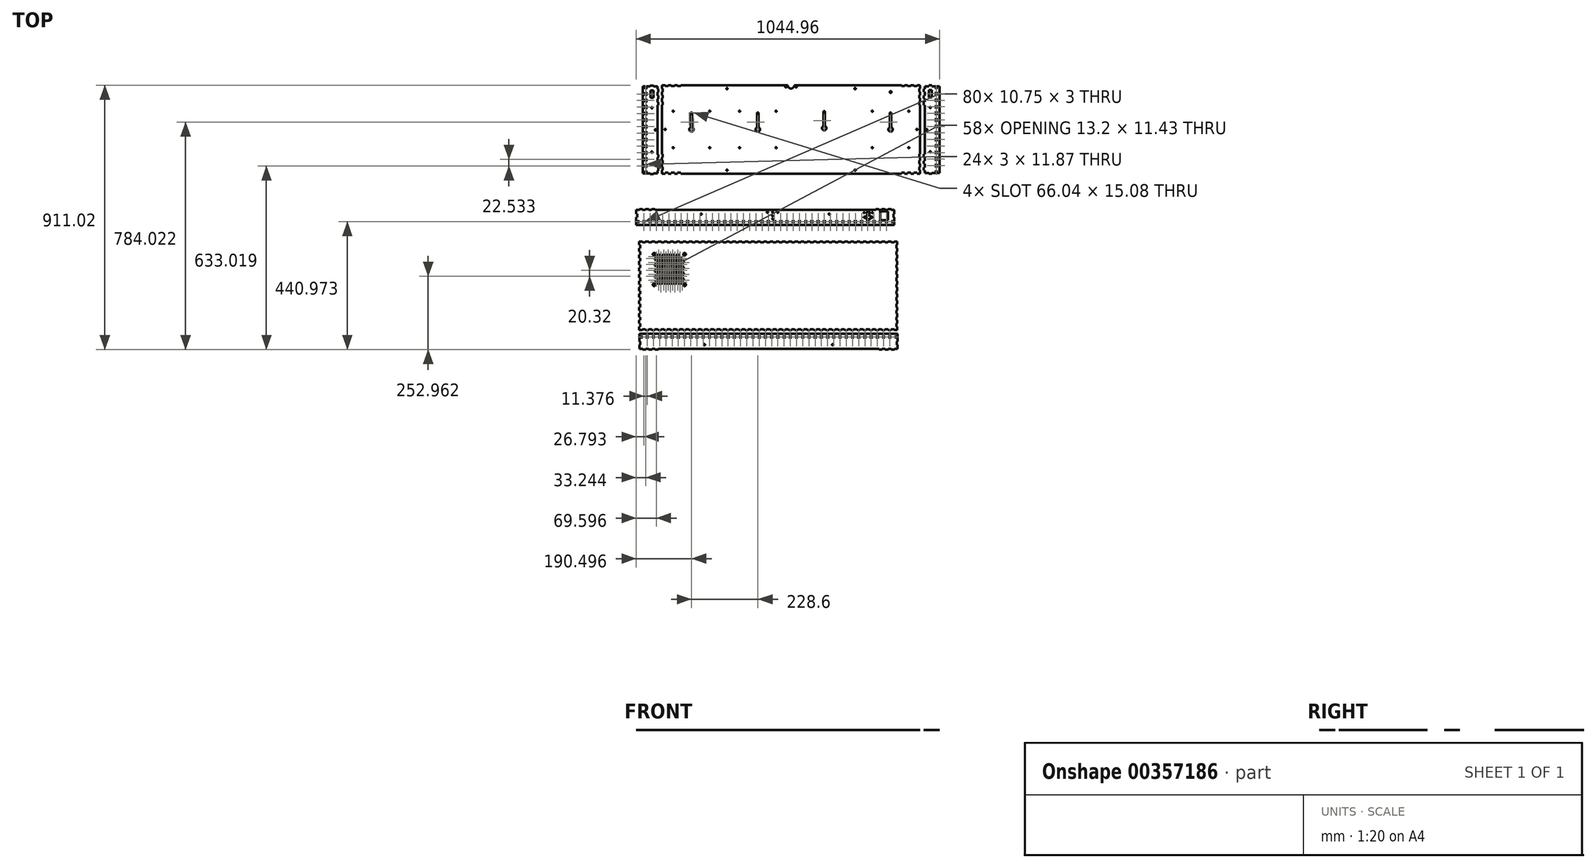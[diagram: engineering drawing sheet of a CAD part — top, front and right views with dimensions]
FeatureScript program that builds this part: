
annotation { "Feature Type Name" : "Feature", "Feature Type Description" : "" }
export const myFeature = defineFeature(function(context is Context, id is Id, definition is map)
    precondition{}
    {
        {
            var Q0;
            Q0=qCreatedBy(makeId("Top.planeOp"),FACE);
            var sketch = newSketch(context, id + "F0", { "sketchPlane" : qUnion([Q0])});
            skLineSegment(sketch, "E0", {"start": v(-511.9, -83.35) * mm, "end": v(-501.15, -83.35) * mm});
            skLineSegment(sketch, "E1", {"start": v(-501.15, -83.35) * mm, "end": v(-501.15, -86.34) * mm});
            skLineSegment(sketch, "E2", {"start": v(-501.15, -86.34) * mm, "end": v(-490.48, -86.34) * mm});
            skLineSegment(sketch, "E3", {"start": v(-490.48, -86.34) * mm, "end": v(-490.48, -83.35) * mm});
            skLineSegment(sketch, "E4", {"start": v(-490.48, -83.35) * mm, "end": v(-479.73, -83.35) * mm});
            skLineSegment(sketch, "E5", {"start": v(-479.73, -83.35) * mm, "end": v(-479.73, -86.34) * mm});
            skLineSegment(sketch, "E6", {"start": v(-479.73, -86.34) * mm, "end": v(-469.06, -86.34) * mm});
            skLineSegment(sketch, "E7", {"start": v(-469.06, -86.34) * mm, "end": v(-469.06, -83.35) * mm});
            skLineSegment(sketch, "E8", {"start": v(-469.06, -83.35) * mm, "end": v(-458.3, -83.35) * mm});
            skLineSegment(sketch, "E9", {"start": v(-458.3, -83.35) * mm, "end": v(-458.3, -86.34) * mm});
            skLineSegment(sketch, "E10", {"start": v(-458.3, -86.34) * mm, "end": v(-447.64, -86.34) * mm});
            skLineSegment(sketch, "E11", {"start": v(-447.64, -86.34) * mm, "end": v(-447.64, -83.35) * mm});
            skLineSegment(sketch, "E12", {"start": v(-447.64, -83.35) * mm, "end": v(-436.89, -83.35) * mm});
            skLineSegment(sketch, "E13", {"start": v(-436.89, -83.35) * mm, "end": v(-436.89, -86.34) * mm});
            skLineSegment(sketch, "E14", {"start": v(-436.89, -86.34) * mm, "end": v(-426.22, -86.34) * mm});
            skLineSegment(sketch, "E15", {"start": v(-426.22, -86.34) * mm, "end": v(-426.22, -83.35) * mm});
            skLineSegment(sketch, "E16", {"start": v(-426.22, -83.35) * mm, "end": v(-415.47, -83.35) * mm});
            skLineSegment(sketch, "E17", {"start": v(-415.47, -83.35) * mm, "end": v(-415.47, -86.34) * mm});
            skLineSegment(sketch, "E18", {"start": v(-415.47, -86.34) * mm, "end": v(-404.8, -86.34) * mm});
            skLineSegment(sketch, "E19", {"start": v(-404.8, -86.34) * mm, "end": v(-404.8, -83.35) * mm});
            skLineSegment(sketch, "E20", {"start": v(-404.8, -83.35) * mm, "end": v(-394.05, -83.35) * mm});
            skLineSegment(sketch, "E21", {"start": v(-394.05, -83.35) * mm, "end": v(-394.05, -86.34) * mm});
            skLineSegment(sketch, "E22", {"start": v(-394.05, -86.34) * mm, "end": v(-383.38, -86.34) * mm});
            skLineSegment(sketch, "E23", {"start": v(-383.38, -86.34) * mm, "end": v(-383.38, -83.35) * mm});
            skLineSegment(sketch, "E24", {"start": v(-383.38, -83.35) * mm, "end": v(-372.62, -83.35) * mm});
            skLineSegment(sketch, "E25", {"start": v(-372.62, -83.35) * mm, "end": v(-372.62, -86.34) * mm});
            skLineSegment(sketch, "E26", {"start": v(-372.62, -86.34) * mm, "end": v(-361.96, -86.34) * mm});
            skLineSegment(sketch, "E27", {"start": v(-361.96, -86.34) * mm, "end": v(-361.96, -83.35) * mm});
            skLineSegment(sketch, "E28", {"start": v(-361.96, -83.35) * mm, "end": v(-351.2, -83.35) * mm});
            skLineSegment(sketch, "E29", {"start": v(-351.2, -83.35) * mm, "end": v(-351.2, -86.34) * mm});
            skLineSegment(sketch, "E30", {"start": v(-351.2, -86.34) * mm, "end": v(-340.54, -86.34) * mm});
            skLineSegment(sketch, "E31", {"start": v(-340.54, -86.34) * mm, "end": v(-340.54, -83.35) * mm});
            skLineSegment(sketch, "E32", {"start": v(-340.54, -83.35) * mm, "end": v(-329.78, -83.35) * mm});
            skLineSegment(sketch, "E33", {"start": v(-329.78, -83.35) * mm, "end": v(-329.78, -86.34) * mm});
            skLineSegment(sketch, "E34", {"start": v(-329.78, -86.34) * mm, "end": v(-319.12, -86.34) * mm});
            skLineSegment(sketch, "E35", {"start": v(-319.12, -86.34) * mm, "end": v(-319.12, -83.35) * mm});
            skLineSegment(sketch, "E36", {"start": v(-319.12, -83.35) * mm, "end": v(-308.36, -83.35) * mm});
            skLineSegment(sketch, "E37", {"start": v(-308.36, -83.35) * mm, "end": v(-308.36, -86.34) * mm});
            skLineSegment(sketch, "E38", {"start": v(-308.36, -86.34) * mm, "end": v(-297.7, -86.34) * mm});
            skLineSegment(sketch, "E39", {"start": v(-297.7, -86.34) * mm, "end": v(-297.7, -83.35) * mm});
            skLineSegment(sketch, "E40", {"start": v(-297.7, -83.35) * mm, "end": v(-286.94, -83.35) * mm});
            skLineSegment(sketch, "E41", {"start": v(-286.94, -83.35) * mm, "end": v(-286.94, -86.34) * mm});
            skLineSegment(sketch, "E42", {"start": v(-286.94, -86.34) * mm, "end": v(-276.27, -86.34) * mm});
            skLineSegment(sketch, "E43", {"start": v(-276.27, -86.34) * mm, "end": v(-276.27, -83.35) * mm});
            skLineSegment(sketch, "E44", {"start": v(-276.27, -83.35) * mm, "end": v(-265.52, -83.35) * mm});
            skLineSegment(sketch, "E45", {"start": v(-265.52, -83.35) * mm, "end": v(-265.52, -86.34) * mm});
            skLineSegment(sketch, "E46", {"start": v(-265.52, -86.34) * mm, "end": v(-254.85, -86.34) * mm});
            skLineSegment(sketch, "E47", {"start": v(-254.85, -86.34) * mm, "end": v(-254.85, -83.35) * mm});
            skLineSegment(sketch, "E48", {"start": v(-254.85, -83.35) * mm, "end": v(-244.1, -83.35) * mm});
            skLineSegment(sketch, "E49", {"start": v(-244.1, -83.35) * mm, "end": v(-244.1, -86.34) * mm});
            skLineSegment(sketch, "E50", {"start": v(-244.1, -86.34) * mm, "end": v(-233.43, -86.34) * mm});
            skLineSegment(sketch, "E51", {"start": v(-233.43, -86.34) * mm, "end": v(-233.43, -83.35) * mm});
            skLineSegment(sketch, "E52", {"start": v(-233.43, -83.35) * mm, "end": v(-222.68, -83.35) * mm});
            skLineSegment(sketch, "E53", {"start": v(-222.68, -83.35) * mm, "end": v(-222.68, -86.34) * mm});
            skLineSegment(sketch, "E54", {"start": v(-222.68, -86.34) * mm, "end": v(-212.01, -86.34) * mm});
            skLineSegment(sketch, "E55", {"start": v(-212.01, -86.34) * mm, "end": v(-212.01, -83.35) * mm});
            skLineSegment(sketch, "E56", {"start": v(-212.01, -83.35) * mm, "end": v(-201.26, -83.35) * mm});
            skLineSegment(sketch, "E57", {"start": v(-201.26, -83.35) * mm, "end": v(-201.26, -86.34) * mm});
            skLineSegment(sketch, "E58", {"start": v(-201.26, -86.34) * mm, "end": v(-190.6, -86.34) * mm});
            skLineSegment(sketch, "E59", {"start": v(-190.6, -86.34) * mm, "end": v(-190.6, -83.35) * mm});
            skLineSegment(sketch, "E60", {"start": v(-190.6, -83.35) * mm, "end": v(-179.84, -83.35) * mm});
            skLineSegment(sketch, "E61", {"start": v(-179.84, -83.35) * mm, "end": v(-179.84, -86.34) * mm});
            skLineSegment(sketch, "E62", {"start": v(-179.84, -86.34) * mm, "end": v(-169.17, -86.34) * mm});
            skLineSegment(sketch, "E63", {"start": v(-169.17, -86.34) * mm, "end": v(-169.17, -83.35) * mm});
            skLineSegment(sketch, "E64", {"start": v(-169.17, -83.35) * mm, "end": v(-158.42, -83.35) * mm});
            skLineSegment(sketch, "E65", {"start": v(-158.42, -83.35) * mm, "end": v(-158.42, -86.34) * mm});
            skLineSegment(sketch, "E66", {"start": v(-158.42, -86.34) * mm, "end": v(-147.75, -86.34) * mm});
            skLineSegment(sketch, "E67", {"start": v(-147.75, -86.34) * mm, "end": v(-147.75, -83.35) * mm});
            skLineSegment(sketch, "E68", {"start": v(-147.75, -83.35) * mm, "end": v(-137, -83.35) * mm});
            skLineSegment(sketch, "E69", {"start": v(-137, -83.35) * mm, "end": v(-137, -86.34) * mm});
            skLineSegment(sketch, "E70", {"start": v(-137, -86.34) * mm, "end": v(-126.33, -86.34) * mm});
            skLineSegment(sketch, "E71", {"start": v(-126.33, -86.34) * mm, "end": v(-126.33, -83.35) * mm});
            skLineSegment(sketch, "E72", {"start": v(-126.33, -83.35) * mm, "end": v(-115.58, -83.35) * mm});
            skLineSegment(sketch, "E73", {"start": v(-115.58, -83.35) * mm, "end": v(-115.58, -86.34) * mm});
            skLineSegment(sketch, "E74", {"start": v(-115.58, -86.34) * mm, "end": v(-104.9, -86.34) * mm});
            skLineSegment(sketch, "E75", {"start": v(-104.9, -86.34) * mm, "end": v(-104.9, -83.35) * mm});
            skLineSegment(sketch, "E76", {"start": v(-104.9, -83.35) * mm, "end": v(-94.16, -83.35) * mm});
            skLineSegment(sketch, "E77", {"start": v(-94.16, -83.35) * mm, "end": v(-94.16, -86.34) * mm});
            skLineSegment(sketch, "E78", {"start": v(-94.16, -86.34) * mm, "end": v(-83.49, -86.34) * mm});
            skLineSegment(sketch, "E79", {"start": v(-83.49, -86.34) * mm, "end": v(-83.49, -83.35) * mm});
            skLineSegment(sketch, "E80", {"start": v(-83.49, -83.35) * mm, "end": v(-72.74, -83.35) * mm});
            skLineSegment(sketch, "E81", {"start": v(-72.74, -83.35) * mm, "end": v(-72.74, -86.34) * mm});
            skLineSegment(sketch, "E82", {"start": v(-72.74, -86.34) * mm, "end": v(-62.07, -86.34) * mm});
            skLineSegment(sketch, "E83", {"start": v(-62.07, -86.34) * mm, "end": v(-62.07, -83.35) * mm});
            skLineSegment(sketch, "E84", {"start": v(-62.07, -83.35) * mm, "end": v(-51.31, -83.35) * mm});
            skLineSegment(sketch, "E85", {"start": v(-51.31, -83.35) * mm, "end": v(-51.31, -86.34) * mm});
            skLineSegment(sketch, "E86", {"start": v(-51.31, -86.34) * mm, "end": v(-40.65, -86.34) * mm});
            skLineSegment(sketch, "E87", {"start": v(-40.65, -86.34) * mm, "end": v(-40.65, -83.35) * mm});
            skLineSegment(sketch, "E88", {"start": v(-40.65, -83.35) * mm, "end": v(-29.9, -83.35) * mm});
            skLineSegment(sketch, "E89", {"start": v(-29.9, -83.35) * mm, "end": v(-29.9, -86.34) * mm});
            skLineSegment(sketch, "E90", {"start": v(-29.9, -86.34) * mm, "end": v(-19.23, -86.34) * mm});
            skLineSegment(sketch, "E91", {"start": v(-19.23, -86.34) * mm, "end": v(-19.23, -83.35) * mm});
            skLineSegment(sketch, "E92", {"start": v(-19.23, -83.35) * mm, "end": v(-8.47, -83.35) * mm});
            skLineSegment(sketch, "E93", {"start": v(-8.47, -83.35) * mm, "end": v(-8.47, -86.34) * mm});
            skLineSegment(sketch, "E94", {"start": v(-8.47, -86.34) * mm, "end": v(2.2, -86.34) * mm});
            skLineSegment(sketch, "E95", {"start": v(2.2, -86.34) * mm, "end": v(2.2, -83.35) * mm});
            skLineSegment(sketch, "E96", {"start": v(2.2, -83.35) * mm, "end": v(12.95, -83.35) * mm});
            skLineSegment(sketch, "E97", {"start": v(12.95, -83.35) * mm, "end": v(12.95, -86.34) * mm});
            skLineSegment(sketch, "E98", {"start": v(12.95, -86.34) * mm, "end": v(23.62, -86.34) * mm});
            skLineSegment(sketch, "E99", {"start": v(23.62, -86.34) * mm, "end": v(23.62, -83.35) * mm});
            skLineSegment(sketch, "E100", {"start": v(23.62, -83.35) * mm, "end": v(34.37, -83.35) * mm});
            skLineSegment(sketch, "E101", {"start": v(34.37, -83.35) * mm, "end": v(34.37, -86.34) * mm});
            skLineSegment(sketch, "E102", {"start": v(34.37, -86.34) * mm, "end": v(45.04, -86.34) * mm});
            skLineSegment(sketch, "E103", {"start": v(45.04, -86.34) * mm, "end": v(45.04, -83.35) * mm});
            skLineSegment(sketch, "E104", {"start": v(45.04, -83.35) * mm, "end": v(55.79, -83.35) * mm});
            skLineSegment(sketch, "E105", {"start": v(55.79, -83.35) * mm, "end": v(55.79, -86.34) * mm});
            skLineSegment(sketch, "E106", {"start": v(55.79, -86.34) * mm, "end": v(66.46, -86.34) * mm});
            skLineSegment(sketch, "E107", {"start": v(66.46, -86.34) * mm, "end": v(66.46, -83.35) * mm});
            skLineSegment(sketch, "E108", {"start": v(66.46, -83.35) * mm, "end": v(77.2, -83.35) * mm});
            skLineSegment(sketch, "E109", {"start": v(77.2, -83.35) * mm, "end": v(77.2, -86.34) * mm});
            skLineSegment(sketch, "E110", {"start": v(77.2, -86.34) * mm, "end": v(87.88, -86.34) * mm});
            skLineSegment(sketch, "E111", {"start": v(87.88, -86.34) * mm, "end": v(87.88, -83.35) * mm});
            skLineSegment(sketch, "E112", {"start": v(87.88, -83.35) * mm, "end": v(98.63, -83.35) * mm});
            skLineSegment(sketch, "E113", {"start": v(98.63, -83.35) * mm, "end": v(98.63, -86.34) * mm});
            skLineSegment(sketch, "E114", {"start": v(98.63, -86.34) * mm, "end": v(109.3, -86.34) * mm});
            skLineSegment(sketch, "E115", {"start": v(109.3, -86.34) * mm, "end": v(109.3, -83.35) * mm});
            skLineSegment(sketch, "E116", {"start": v(109.3, -83.35) * mm, "end": v(120.05, -83.35) * mm});
            skLineSegment(sketch, "E117", {"start": v(120.05, -83.35) * mm, "end": v(120.05, -86.34) * mm});
            skLineSegment(sketch, "E118", {"start": v(120.05, -86.34) * mm, "end": v(130.72, -86.34) * mm});
            skLineSegment(sketch, "E119", {"start": v(130.72, -86.34) * mm, "end": v(130.72, -83.35) * mm});
            skLineSegment(sketch, "E120", {"start": v(130.72, -83.35) * mm, "end": v(141.47, -83.35) * mm});
            skLineSegment(sketch, "E121", {"start": v(141.47, -83.35) * mm, "end": v(141.47, -86.34) * mm});
            skLineSegment(sketch, "E122", {"start": v(141.47, -86.34) * mm, "end": v(152.14, -86.34) * mm});
            skLineSegment(sketch, "E123", {"start": v(152.14, -86.34) * mm, "end": v(152.14, -83.35) * mm});
            skLineSegment(sketch, "E124", {"start": v(152.14, -83.35) * mm, "end": v(162.9, -83.35) * mm});
            skLineSegment(sketch, "E125", {"start": v(162.9, -83.35) * mm, "end": v(162.9, -86.34) * mm});
            skLineSegment(sketch, "E126", {"start": v(162.9, -86.34) * mm, "end": v(173.56, -86.34) * mm});
            skLineSegment(sketch, "E127", {"start": v(173.56, -86.34) * mm, "end": v(173.56, -83.35) * mm});
            skLineSegment(sketch, "E128", {"start": v(173.56, -83.35) * mm, "end": v(184.31, -83.35) * mm});
            skLineSegment(sketch, "E129", {"start": v(184.31, -83.35) * mm, "end": v(184.31, -86.34) * mm});
            skLineSegment(sketch, "E130", {"start": v(184.31, -86.34) * mm, "end": v(194.98, -86.34) * mm});
            skLineSegment(sketch, "E131", {"start": v(194.98, -86.34) * mm, "end": v(194.98, -83.35) * mm});
            skLineSegment(sketch, "E132", {"start": v(194.98, -83.35) * mm, "end": v(205.73, -83.35) * mm});
            skLineSegment(sketch, "E133", {"start": v(205.73, -83.35) * mm, "end": v(205.73, -86.34) * mm});
            skLineSegment(sketch, "E134", {"start": v(205.73, -86.34) * mm, "end": v(216.4, -86.34) * mm});
            skLineSegment(sketch, "E135", {"start": v(216.4, -86.34) * mm, "end": v(216.4, -83.35) * mm});
            skLineSegment(sketch, "E136", {"start": v(216.4, -83.35) * mm, "end": v(227.15, -83.35) * mm});
            skLineSegment(sketch, "E137", {"start": v(227.15, -83.35) * mm, "end": v(227.15, -86.34) * mm});
            skLineSegment(sketch, "E138", {"start": v(227.15, -86.34) * mm, "end": v(237.82, -86.34) * mm});
            skLineSegment(sketch, "E139", {"start": v(237.82, -86.34) * mm, "end": v(237.82, -83.35) * mm});
            skLineSegment(sketch, "E140", {"start": v(237.82, -83.35) * mm, "end": v(248.57, -83.35) * mm});
            skLineSegment(sketch, "E141", {"start": v(248.57, -83.35) * mm, "end": v(248.57, -86.34) * mm});
            skLineSegment(sketch, "E142", {"start": v(248.57, -86.34) * mm, "end": v(259.24, -86.34) * mm});
            skLineSegment(sketch, "E143", {"start": v(259.24, -86.34) * mm, "end": v(259.24, -83.35) * mm});
            skLineSegment(sketch, "E144", {"start": v(259.24, -83.35) * mm, "end": v(270, -83.35) * mm});
            skLineSegment(sketch, "E145", {"start": v(270, -83.35) * mm, "end": v(270, -86.34) * mm});
            skLineSegment(sketch, "E146", {"start": v(270, -86.34) * mm, "end": v(280.66, -86.34) * mm});
            skLineSegment(sketch, "E147", {"start": v(280.66, -86.34) * mm, "end": v(280.66, -83.35) * mm});
            skLineSegment(sketch, "E148", {"start": v(280.66, -83.35) * mm, "end": v(291.42, -83.35) * mm});
            skLineSegment(sketch, "E149", {"start": v(291.42, -83.35) * mm, "end": v(291.42, -86.34) * mm});
            skLineSegment(sketch, "E150", {"start": v(291.42, -86.34) * mm, "end": v(302.08, -86.34) * mm});
            skLineSegment(sketch, "E151", {"start": v(302.08, -86.34) * mm, "end": v(302.08, -83.35) * mm});
            skLineSegment(sketch, "E152", {"start": v(302.08, -83.35) * mm, "end": v(312.84, -83.35) * mm});
            skLineSegment(sketch, "E153", {"start": v(312.84, -83.35) * mm, "end": v(312.84, -86.34) * mm});
            skLineSegment(sketch, "E154", {"start": v(312.84, -86.34) * mm, "end": v(323.5, -86.34) * mm});
            skLineSegment(sketch, "E155", {"start": v(323.5, -86.34) * mm, "end": v(323.5, -83.35) * mm});
            skLineSegment(sketch, "E156", {"start": v(323.5, -83.35) * mm, "end": v(334.26, -83.35) * mm});
            skLineSegment(sketch, "E157", {"start": v(334.26, -83.35) * mm, "end": v(334.26, -86.34) * mm});
            skLineSegment(sketch, "E158", {"start": v(334.26, -86.34) * mm, "end": v(344.93, -86.34) * mm});
            skLineSegment(sketch, "E159", {"start": v(344.93, -86.34) * mm, "end": v(344.93, -83.35) * mm});
            skLineSegment(sketch, "E160", {"start": v(344.93, -83.35) * mm, "end": v(355.68, -83.35) * mm});
            skLineSegment(sketch, "E161", {"start": v(355.68, -83.35) * mm, "end": v(355.68, -86.34) * mm});
            skLineSegment(sketch, "E162", {"start": v(355.68, -86.34) * mm, "end": v(366.35, -86.34) * mm});
            skLineSegment(sketch, "E163", {"start": v(366.35, -86.34) * mm, "end": v(366.35, -83.35) * mm});
            skLineSegment(sketch, "E164", {"start": v(366.35, -83.35) * mm, "end": v(377.1, -83.35) * mm});
            skLineSegment(sketch, "E165", {"start": v(377.1, -83.35) * mm, "end": v(377.1, -95.21) * mm});
            skLineSegment(sketch, "E166", {"start": v(377.1, -95.21) * mm, "end": v(374.1, -95.21) * mm});
            skLineSegment(sketch, "E167", {"start": v(374.1, -95.21) * mm, "end": v(374.1, -105.88) * mm});
            skLineSegment(sketch, "E168", {"start": v(374.1, -105.88) * mm, "end": v(377.1, -105.88) * mm});
            skLineSegment(sketch, "E169", {"start": v(377.1, -105.88) * mm, "end": v(377.1, -117.75) * mm});
            skLineSegment(sketch, "E170", {"start": v(377.1, -117.75) * mm, "end": v(374.1, -117.75) * mm});
            skLineSegment(sketch, "E171", {"start": v(374.1, -117.75) * mm, "end": v(374.1, -128.41) * mm});
            skLineSegment(sketch, "E172", {"start": v(374.1, -128.41) * mm, "end": v(377.1, -128.41) * mm});
            skLineSegment(sketch, "E173", {"start": v(377.1, -128.41) * mm, "end": v(377.1, -140.28) * mm});
            skLineSegment(sketch, "E174", {"start": v(377.1, -140.28) * mm, "end": v(374.1, -140.28) * mm});
            skLineSegment(sketch, "E175", {"start": v(374.1, -140.28) * mm, "end": v(374.1, -150.95) * mm});
            skLineSegment(sketch, "E176", {"start": v(374.1, -150.95) * mm, "end": v(377.1, -150.95) * mm});
            skLineSegment(sketch, "E177", {"start": v(377.1, -150.95) * mm, "end": v(377.1, -162.81) * mm});
            skLineSegment(sketch, "E178", {"start": v(377.1, -162.81) * mm, "end": v(374.1, -162.81) * mm});
            skLineSegment(sketch, "E179", {"start": v(374.1, -162.81) * mm, "end": v(374.1, -173.48) * mm});
            skLineSegment(sketch, "E180", {"start": v(374.1, -173.48) * mm, "end": v(377.1, -173.48) * mm});
            skLineSegment(sketch, "E181", {"start": v(377.1, -173.48) * mm, "end": v(377.1, -185.35) * mm});
            skLineSegment(sketch, "E182", {"start": v(377.1, -185.35) * mm, "end": v(374.1, -185.35) * mm});
            skLineSegment(sketch, "E183", {"start": v(374.1, -185.35) * mm, "end": v(374.1, -196.01) * mm});
            skLineSegment(sketch, "E184", {"start": v(374.1, -196.01) * mm, "end": v(377.1, -196.01) * mm});
            skLineSegment(sketch, "E185", {"start": v(377.1, -196.01) * mm, "end": v(377.1, -207.88) * mm});
            skLineSegment(sketch, "E186", {"start": v(377.1, -207.88) * mm, "end": v(374.1, -207.88) * mm});
            skLineSegment(sketch, "E187", {"start": v(374.1, -207.88) * mm, "end": v(374.1, -218.55) * mm});
            skLineSegment(sketch, "E188", {"start": v(374.1, -218.55) * mm, "end": v(377.1, -218.55) * mm});
            skLineSegment(sketch, "E189", {"start": v(377.1, -218.55) * mm, "end": v(377.1, -230.41) * mm});
            skLineSegment(sketch, "E190", {"start": v(377.1, -230.41) * mm, "end": v(374.1, -230.41) * mm});
            skLineSegment(sketch, "E191", {"start": v(374.1, -230.41) * mm, "end": v(374.1, -241.08) * mm});
            skLineSegment(sketch, "E192", {"start": v(374.1, -241.08) * mm, "end": v(377.1, -241.08) * mm});
            skLineSegment(sketch, "E193", {"start": v(377.1, -241.08) * mm, "end": v(377.1, -252.95) * mm});
            skLineSegment(sketch, "E194", {"start": v(377.1, -252.95) * mm, "end": v(374.1, -252.95) * mm});
            skLineSegment(sketch, "E195", {"start": v(374.1, -252.95) * mm, "end": v(374.1, -263.61) * mm});
            skLineSegment(sketch, "E196", {"start": v(374.1, -263.61) * mm, "end": v(377.1, -263.61) * mm});
            skLineSegment(sketch, "E197", {"start": v(377.1, -263.61) * mm, "end": v(377.1, -275.48) * mm});
            skLineSegment(sketch, "E198", {"start": v(377.1, -275.48) * mm, "end": v(374.1, -275.48) * mm});
            skLineSegment(sketch, "E199", {"start": v(374.1, -275.48) * mm, "end": v(374.1, -286.15) * mm});
            skLineSegment(sketch, "E200", {"start": v(374.1, -286.15) * mm, "end": v(377.1, -286.15) * mm});
            skLineSegment(sketch, "E201", {"start": v(377.1, -286.15) * mm, "end": v(377.1, -298.01) * mm});
            skLineSegment(sketch, "E202", {"start": v(377.1, -298.01) * mm, "end": v(374.1, -298.01) * mm});
            skLineSegment(sketch, "E203", {"start": v(374.1, -298.01) * mm, "end": v(374.1, -308.68) * mm});
            skLineSegment(sketch, "E204", {"start": v(374.1, -308.68) * mm, "end": v(377.1, -308.68) * mm});
            skLineSegment(sketch, "E205", {"start": v(377.1, -308.68) * mm, "end": v(377.1, -320.55) * mm});
            skLineSegment(sketch, "E206", {"start": v(377.1, -320.55) * mm, "end": v(374.1, -320.55) * mm});
            skLineSegment(sketch, "E207", {"start": v(374.1, -320.55) * mm, "end": v(374.1, -331.22) * mm});
            skLineSegment(sketch, "E208", {"start": v(374.1, -331.22) * mm, "end": v(377.1, -331.22) * mm});
            skLineSegment(sketch, "E209", {"start": v(377.1, -331.22) * mm, "end": v(377.1, -343.08) * mm});
            skLineSegment(sketch, "E210", {"start": v(377.1, -343.08) * mm, "end": v(374.1, -343.08) * mm});
            skLineSegment(sketch, "E211", {"start": v(374.1, -343.08) * mm, "end": v(374.1, -353.75) * mm});
            skLineSegment(sketch, "E212", {"start": v(374.1, -353.75) * mm, "end": v(377.1, -353.75) * mm});
            skLineSegment(sketch, "E213", {"start": v(377.1, -353.75) * mm, "end": v(377.1, -365.61) * mm});
            skLineSegment(sketch, "E214", {"start": v(377.1, -365.61) * mm, "end": v(374.1, -365.61) * mm});
            skLineSegment(sketch, "E215", {"start": v(374.1, -365.61) * mm, "end": v(374.1, -376.28) * mm});
            skLineSegment(sketch, "E216", {"start": v(374.1, -376.28) * mm, "end": v(377.1, -376.28) * mm});
            skLineSegment(sketch, "E217", {"start": v(377.1, -376.28) * mm, "end": v(377.1, -388.15) * mm});
            skLineSegment(sketch, "E218", {"start": v(377.1, -388.15) * mm, "end": v(366.35, -388.15) * mm});
            skLineSegment(sketch, "E219", {"start": v(366.35, -388.15) * mm, "end": v(366.35, -385.15) * mm});
            skLineSegment(sketch, "E220", {"start": v(366.35, -385.15) * mm, "end": v(355.68, -385.15) * mm});
            skLineSegment(sketch, "E221", {"start": v(355.68, -385.15) * mm, "end": v(355.68, -388.15) * mm});
            skLineSegment(sketch, "E222", {"start": v(355.68, -388.15) * mm, "end": v(344.93, -388.15) * mm});
            skLineSegment(sketch, "E223", {"start": v(344.93, -388.15) * mm, "end": v(344.93, -385.15) * mm});
            skLineSegment(sketch, "E224", {"start": v(344.93, -385.15) * mm, "end": v(334.26, -385.15) * mm});
            skLineSegment(sketch, "E225", {"start": v(334.26, -385.15) * mm, "end": v(334.26, -388.15) * mm});
            skLineSegment(sketch, "E226", {"start": v(334.26, -388.15) * mm, "end": v(323.5, -388.15) * mm});
            skLineSegment(sketch, "E227", {"start": v(323.5, -388.15) * mm, "end": v(323.5, -385.15) * mm});
            skLineSegment(sketch, "E228", {"start": v(323.5, -385.15) * mm, "end": v(312.84, -385.15) * mm});
            skLineSegment(sketch, "E229", {"start": v(312.84, -385.15) * mm, "end": v(312.84, -388.15) * mm});
            skLineSegment(sketch, "E230", {"start": v(312.84, -388.15) * mm, "end": v(302.08, -388.15) * mm});
            skLineSegment(sketch, "E231", {"start": v(302.08, -388.15) * mm, "end": v(302.08, -385.15) * mm});
            skLineSegment(sketch, "E232", {"start": v(302.08, -385.15) * mm, "end": v(291.42, -385.15) * mm});
            skLineSegment(sketch, "E233", {"start": v(291.42, -385.15) * mm, "end": v(291.42, -388.15) * mm});
            skLineSegment(sketch, "E234", {"start": v(291.42, -388.15) * mm, "end": v(280.66, -388.15) * mm});
            skLineSegment(sketch, "E235", {"start": v(280.66, -388.15) * mm, "end": v(280.66, -385.15) * mm});
            skLineSegment(sketch, "E236", {"start": v(280.66, -385.15) * mm, "end": v(270, -385.15) * mm});
            skLineSegment(sketch, "E237", {"start": v(270, -385.15) * mm, "end": v(270, -388.15) * mm});
            skLineSegment(sketch, "E238", {"start": v(270, -388.15) * mm, "end": v(259.24, -388.15) * mm});
            skLineSegment(sketch, "E239", {"start": v(259.24, -388.15) * mm, "end": v(259.24, -385.15) * mm});
            skLineSegment(sketch, "E240", {"start": v(259.24, -385.15) * mm, "end": v(248.57, -385.15) * mm});
            skLineSegment(sketch, "E241", {"start": v(248.57, -385.15) * mm, "end": v(248.57, -388.15) * mm});
            skLineSegment(sketch, "E242", {"start": v(248.57, -388.15) * mm, "end": v(237.82, -388.15) * mm});
            skLineSegment(sketch, "E243", {"start": v(237.82, -388.15) * mm, "end": v(237.82, -385.15) * mm});
            skLineSegment(sketch, "E244", {"start": v(237.82, -385.15) * mm, "end": v(227.15, -385.15) * mm});
            skLineSegment(sketch, "E245", {"start": v(227.15, -385.15) * mm, "end": v(227.15, -388.15) * mm});
            skLineSegment(sketch, "E246", {"start": v(227.15, -388.15) * mm, "end": v(216.4, -388.15) * mm});
            skLineSegment(sketch, "E247", {"start": v(216.4, -388.15) * mm, "end": v(216.4, -385.15) * mm});
            skLineSegment(sketch, "E248", {"start": v(216.4, -385.15) * mm, "end": v(205.73, -385.15) * mm});
            skLineSegment(sketch, "E249", {"start": v(205.73, -385.15) * mm, "end": v(205.73, -388.15) * mm});
            skLineSegment(sketch, "E250", {"start": v(205.73, -388.15) * mm, "end": v(194.98, -388.15) * mm});
            skLineSegment(sketch, "E251", {"start": v(194.98, -388.15) * mm, "end": v(194.98, -385.15) * mm});
            skLineSegment(sketch, "E252", {"start": v(194.98, -385.15) * mm, "end": v(184.31, -385.15) * mm});
            skLineSegment(sketch, "E253", {"start": v(184.31, -385.15) * mm, "end": v(184.31, -388.15) * mm});
            skLineSegment(sketch, "E254", {"start": v(184.31, -388.15) * mm, "end": v(173.56, -388.15) * mm});
            skLineSegment(sketch, "E255", {"start": v(173.56, -388.15) * mm, "end": v(173.56, -385.15) * mm});
            skLineSegment(sketch, "E256", {"start": v(173.56, -385.15) * mm, "end": v(162.9, -385.15) * mm});
            skLineSegment(sketch, "E257", {"start": v(162.9, -385.15) * mm, "end": v(162.9, -388.15) * mm});
            skLineSegment(sketch, "E258", {"start": v(162.9, -388.15) * mm, "end": v(152.14, -388.15) * mm});
            skLineSegment(sketch, "E259", {"start": v(152.14, -388.15) * mm, "end": v(152.14, -385.15) * mm});
            skLineSegment(sketch, "E260", {"start": v(152.14, -385.15) * mm, "end": v(141.47, -385.15) * mm});
            skLineSegment(sketch, "E261", {"start": v(141.47, -385.15) * mm, "end": v(141.47, -388.15) * mm});
            skLineSegment(sketch, "E262", {"start": v(141.47, -388.15) * mm, "end": v(130.72, -388.15) * mm});
            skLineSegment(sketch, "E263", {"start": v(130.72, -388.15) * mm, "end": v(130.72, -385.15) * mm});
            skLineSegment(sketch, "E264", {"start": v(130.72, -385.15) * mm, "end": v(120.05, -385.15) * mm});
            skLineSegment(sketch, "E265", {"start": v(120.05, -385.15) * mm, "end": v(120.05, -388.15) * mm});
            skLineSegment(sketch, "E266", {"start": v(120.05, -388.15) * mm, "end": v(109.3, -388.15) * mm});
            skLineSegment(sketch, "E267", {"start": v(109.3, -388.15) * mm, "end": v(109.3, -385.15) * mm});
            skLineSegment(sketch, "E268", {"start": v(109.3, -385.15) * mm, "end": v(98.63, -385.15) * mm});
            skLineSegment(sketch, "E269", {"start": v(98.63, -385.15) * mm, "end": v(98.63, -388.15) * mm});
            skLineSegment(sketch, "E270", {"start": v(98.63, -388.15) * mm, "end": v(87.88, -388.15) * mm});
            skLineSegment(sketch, "E271", {"start": v(87.88, -388.15) * mm, "end": v(87.88, -385.15) * mm});
            skLineSegment(sketch, "E272", {"start": v(87.88, -385.15) * mm, "end": v(77.2, -385.15) * mm});
            skLineSegment(sketch, "E273", {"start": v(77.2, -385.15) * mm, "end": v(77.2, -388.15) * mm});
            skLineSegment(sketch, "E274", {"start": v(77.2, -388.15) * mm, "end": v(66.46, -388.15) * mm});
            skLineSegment(sketch, "E275", {"start": v(66.46, -388.15) * mm, "end": v(66.46, -385.15) * mm});
            skLineSegment(sketch, "E276", {"start": v(66.46, -385.15) * mm, "end": v(55.79, -385.15) * mm});
            skLineSegment(sketch, "E277", {"start": v(55.79, -385.15) * mm, "end": v(55.79, -388.15) * mm});
            skLineSegment(sketch, "E278", {"start": v(55.79, -388.15) * mm, "end": v(45.04, -388.15) * mm});
            skLineSegment(sketch, "E279", {"start": v(45.04, -388.15) * mm, "end": v(45.04, -385.15) * mm});
            skLineSegment(sketch, "E280", {"start": v(45.04, -385.15) * mm, "end": v(34.37, -385.15) * mm});
            skLineSegment(sketch, "E281", {"start": v(34.37, -385.15) * mm, "end": v(34.37, -388.15) * mm});
            skLineSegment(sketch, "E282", {"start": v(34.37, -388.15) * mm, "end": v(23.62, -388.15) * mm});
            skLineSegment(sketch, "E283", {"start": v(23.62, -388.15) * mm, "end": v(23.62, -385.15) * mm});
            skLineSegment(sketch, "E284", {"start": v(23.62, -385.15) * mm, "end": v(12.95, -385.15) * mm});
            skLineSegment(sketch, "E285", {"start": v(12.95, -385.15) * mm, "end": v(12.95, -388.15) * mm});
            skLineSegment(sketch, "E286", {"start": v(12.95, -388.15) * mm, "end": v(2.2, -388.15) * mm});
            skLineSegment(sketch, "E287", {"start": v(2.2, -388.15) * mm, "end": v(2.2, -385.15) * mm});
            skLineSegment(sketch, "E288", {"start": v(2.2, -385.15) * mm, "end": v(-8.47, -385.15) * mm});
            skLineSegment(sketch, "E289", {"start": v(-8.47, -385.15) * mm, "end": v(-8.47, -388.15) * mm});
            skLineSegment(sketch, "E290", {"start": v(-8.47, -388.15) * mm, "end": v(-19.23, -388.15) * mm});
            skLineSegment(sketch, "E291", {"start": v(-19.23, -388.15) * mm, "end": v(-19.23, -385.15) * mm});
            skLineSegment(sketch, "E292", {"start": v(-19.23, -385.15) * mm, "end": v(-29.9, -385.15) * mm});
            skLineSegment(sketch, "E293", {"start": v(-29.9, -385.15) * mm, "end": v(-29.9, -388.15) * mm});
            skLineSegment(sketch, "E294", {"start": v(-29.9, -388.15) * mm, "end": v(-40.65, -388.15) * mm});
            skLineSegment(sketch, "E295", {"start": v(-40.65, -388.15) * mm, "end": v(-40.65, -385.15) * mm});
            skLineSegment(sketch, "E296", {"start": v(-40.65, -385.15) * mm, "end": v(-51.31, -385.15) * mm});
            skLineSegment(sketch, "E297", {"start": v(-51.31, -385.15) * mm, "end": v(-51.31, -388.15) * mm});
            skLineSegment(sketch, "E298", {"start": v(-51.31, -388.15) * mm, "end": v(-62.07, -388.15) * mm});
            skLineSegment(sketch, "E299", {"start": v(-62.07, -388.15) * mm, "end": v(-62.07, -385.15) * mm});
            skLineSegment(sketch, "E300", {"start": v(-62.07, -385.15) * mm, "end": v(-72.74, -385.15) * mm});
            skLineSegment(sketch, "E301", {"start": v(-72.74, -385.15) * mm, "end": v(-72.74, -388.15) * mm});
            skLineSegment(sketch, "E302", {"start": v(-72.74, -388.15) * mm, "end": v(-83.49, -388.15) * mm});
            skLineSegment(sketch, "E303", {"start": v(-83.49, -388.15) * mm, "end": v(-83.49, -385.15) * mm});
            skLineSegment(sketch, "E304", {"start": v(-83.49, -385.15) * mm, "end": v(-94.16, -385.15) * mm});
            skLineSegment(sketch, "E305", {"start": v(-94.16, -385.15) * mm, "end": v(-94.16, -388.15) * mm});
            skLineSegment(sketch, "E306", {"start": v(-94.16, -388.15) * mm, "end": v(-104.9, -388.15) * mm});
            skLineSegment(sketch, "E307", {"start": v(-104.9, -388.15) * mm, "end": v(-104.9, -385.15) * mm});
            skLineSegment(sketch, "E308", {"start": v(-104.9, -385.15) * mm, "end": v(-115.58, -385.15) * mm});
            skLineSegment(sketch, "E309", {"start": v(-115.58, -385.15) * mm, "end": v(-115.58, -388.15) * mm});
            skLineSegment(sketch, "E310", {"start": v(-115.58, -388.15) * mm, "end": v(-126.33, -388.15) * mm});
            skLineSegment(sketch, "E311", {"start": v(-126.33, -388.15) * mm, "end": v(-126.33, -385.15) * mm});
            skLineSegment(sketch, "E312", {"start": v(-126.33, -385.15) * mm, "end": v(-137, -385.15) * mm});
            skLineSegment(sketch, "E313", {"start": v(-137, -385.15) * mm, "end": v(-137, -388.15) * mm});
            skLineSegment(sketch, "E314", {"start": v(-137, -388.15) * mm, "end": v(-147.75, -388.15) * mm});
            skLineSegment(sketch, "E315", {"start": v(-147.75, -388.15) * mm, "end": v(-147.75, -385.15) * mm});
            skLineSegment(sketch, "E316", {"start": v(-147.75, -385.15) * mm, "end": v(-158.42, -385.15) * mm});
            skLineSegment(sketch, "E317", {"start": v(-158.42, -385.15) * mm, "end": v(-158.42, -388.15) * mm});
            skLineSegment(sketch, "E318", {"start": v(-158.42, -388.15) * mm, "end": v(-169.17, -388.15) * mm});
            skLineSegment(sketch, "E319", {"start": v(-169.17, -388.15) * mm, "end": v(-169.17, -385.15) * mm});
            skLineSegment(sketch, "E320", {"start": v(-169.17, -385.15) * mm, "end": v(-179.84, -385.15) * mm});
            skLineSegment(sketch, "E321", {"start": v(-179.84, -385.15) * mm, "end": v(-179.84, -388.15) * mm});
            skLineSegment(sketch, "E322", {"start": v(-179.84, -388.15) * mm, "end": v(-190.6, -388.15) * mm});
            skLineSegment(sketch, "E323", {"start": v(-190.6, -388.15) * mm, "end": v(-190.6, -385.15) * mm});
            skLineSegment(sketch, "E324", {"start": v(-190.6, -385.15) * mm, "end": v(-201.26, -385.15) * mm});
            skLineSegment(sketch, "E325", {"start": v(-201.26, -385.15) * mm, "end": v(-201.26, -388.15) * mm});
            skLineSegment(sketch, "E326", {"start": v(-201.26, -388.15) * mm, "end": v(-212.01, -388.15) * mm});
            skLineSegment(sketch, "E327", {"start": v(-212.01, -388.15) * mm, "end": v(-212.01, -385.15) * mm});
            skLineSegment(sketch, "E328", {"start": v(-212.01, -385.15) * mm, "end": v(-222.68, -385.15) * mm});
            skLineSegment(sketch, "E329", {"start": v(-222.68, -385.15) * mm, "end": v(-222.68, -388.15) * mm});
            skLineSegment(sketch, "E330", {"start": v(-222.68, -388.15) * mm, "end": v(-233.43, -388.15) * mm});
            skLineSegment(sketch, "E331", {"start": v(-233.43, -388.15) * mm, "end": v(-233.43, -385.15) * mm});
            skLineSegment(sketch, "E332", {"start": v(-233.43, -385.15) * mm, "end": v(-244.1, -385.15) * mm});
            skLineSegment(sketch, "E333", {"start": v(-244.1, -385.15) * mm, "end": v(-244.1, -388.15) * mm});
            skLineSegment(sketch, "E334", {"start": v(-244.1, -388.15) * mm, "end": v(-254.85, -388.15) * mm});
            skLineSegment(sketch, "E335", {"start": v(-254.85, -388.15) * mm, "end": v(-254.85, -385.15) * mm});
            skLineSegment(sketch, "E336", {"start": v(-254.85, -385.15) * mm, "end": v(-265.52, -385.15) * mm});
            skLineSegment(sketch, "E337", {"start": v(-265.52, -385.15) * mm, "end": v(-265.52, -388.15) * mm});
            skLineSegment(sketch, "E338", {"start": v(-265.52, -388.15) * mm, "end": v(-276.27, -388.15) * mm});
            skLineSegment(sketch, "E339", {"start": v(-276.27, -388.15) * mm, "end": v(-276.27, -385.15) * mm});
            skLineSegment(sketch, "E340", {"start": v(-276.27, -385.15) * mm, "end": v(-286.94, -385.15) * mm});
            skLineSegment(sketch, "E341", {"start": v(-286.94, -385.15) * mm, "end": v(-286.94, -388.15) * mm});
            skLineSegment(sketch, "E342", {"start": v(-286.94, -388.15) * mm, "end": v(-297.7, -388.15) * mm});
            skLineSegment(sketch, "E343", {"start": v(-297.7, -388.15) * mm, "end": v(-297.7, -385.15) * mm});
            skLineSegment(sketch, "E344", {"start": v(-297.7, -385.15) * mm, "end": v(-308.36, -385.15) * mm});
            skLineSegment(sketch, "E345", {"start": v(-308.36, -385.15) * mm, "end": v(-308.36, -388.15) * mm});
            skLineSegment(sketch, "E346", {"start": v(-308.36, -388.15) * mm, "end": v(-319.12, -388.15) * mm});
            skLineSegment(sketch, "E347", {"start": v(-319.12, -388.15) * mm, "end": v(-319.12, -385.15) * mm});
            skLineSegment(sketch, "E348", {"start": v(-319.12, -385.15) * mm, "end": v(-329.78, -385.15) * mm});
            skLineSegment(sketch, "E349", {"start": v(-329.78, -385.15) * mm, "end": v(-329.78, -388.15) * mm});
            skLineSegment(sketch, "E350", {"start": v(-329.78, -388.15) * mm, "end": v(-340.54, -388.15) * mm});
            skLineSegment(sketch, "E351", {"start": v(-340.54, -388.15) * mm, "end": v(-340.54, -385.15) * mm});
            skLineSegment(sketch, "E352", {"start": v(-340.54, -385.15) * mm, "end": v(-351.2, -385.15) * mm});
            skLineSegment(sketch, "E353", {"start": v(-351.2, -385.15) * mm, "end": v(-351.2, -388.15) * mm});
            skLineSegment(sketch, "E354", {"start": v(-351.2, -388.15) * mm, "end": v(-361.96, -388.15) * mm});
            skLineSegment(sketch, "E355", {"start": v(-361.96, -388.15) * mm, "end": v(-361.96, -385.15) * mm});
            skLineSegment(sketch, "E356", {"start": v(-361.96, -385.15) * mm, "end": v(-372.62, -385.15) * mm});
            skLineSegment(sketch, "E357", {"start": v(-372.62, -385.15) * mm, "end": v(-372.62, -388.15) * mm});
            skLineSegment(sketch, "E358", {"start": v(-372.62, -388.15) * mm, "end": v(-383.38, -388.15) * mm});
            skLineSegment(sketch, "E359", {"start": v(-383.38, -388.15) * mm, "end": v(-383.38, -385.15) * mm});
            skLineSegment(sketch, "E360", {"start": v(-383.38, -385.15) * mm, "end": v(-394.05, -385.15) * mm});
            skLineSegment(sketch, "E361", {"start": v(-394.05, -385.15) * mm, "end": v(-394.05, -388.15) * mm});
            skLineSegment(sketch, "E362", {"start": v(-394.05, -388.15) * mm, "end": v(-404.8, -388.15) * mm});
            skLineSegment(sketch, "E363", {"start": v(-404.8, -388.15) * mm, "end": v(-404.8, -385.15) * mm});
            skLineSegment(sketch, "E364", {"start": v(-404.8, -385.15) * mm, "end": v(-415.47, -385.15) * mm});
            skLineSegment(sketch, "E365", {"start": v(-415.47, -385.15) * mm, "end": v(-415.47, -388.15) * mm});
            skLineSegment(sketch, "E366", {"start": v(-415.47, -388.15) * mm, "end": v(-426.22, -388.15) * mm});
            skLineSegment(sketch, "E367", {"start": v(-426.22, -388.15) * mm, "end": v(-426.22, -385.15) * mm});
            skLineSegment(sketch, "E368", {"start": v(-426.22, -385.15) * mm, "end": v(-436.89, -385.15) * mm});
            skLineSegment(sketch, "E369", {"start": v(-436.89, -385.15) * mm, "end": v(-436.89, -388.15) * mm});
            skLineSegment(sketch, "E370", {"start": v(-436.89, -388.15) * mm, "end": v(-447.64, -388.15) * mm});
            skLineSegment(sketch, "E371", {"start": v(-447.64, -388.15) * mm, "end": v(-447.64, -385.15) * mm});
            skLineSegment(sketch, "E372", {"start": v(-447.64, -385.15) * mm, "end": v(-458.3, -385.15) * mm});
            skLineSegment(sketch, "E373", {"start": v(-458.3, -385.15) * mm, "end": v(-458.3, -388.15) * mm});
            skLineSegment(sketch, "E374", {"start": v(-458.3, -388.15) * mm, "end": v(-469.06, -388.15) * mm});
            skLineSegment(sketch, "E375", {"start": v(-469.06, -388.15) * mm, "end": v(-469.06, -385.15) * mm});
            skLineSegment(sketch, "E376", {"start": v(-469.06, -385.15) * mm, "end": v(-479.73, -385.15) * mm});
            skLineSegment(sketch, "E377", {"start": v(-479.73, -385.15) * mm, "end": v(-479.73, -388.15) * mm});
            skLineSegment(sketch, "E378", {"start": v(-479.73, -388.15) * mm, "end": v(-490.48, -388.15) * mm});
            skLineSegment(sketch, "E379", {"start": v(-490.48, -388.15) * mm, "end": v(-490.48, -385.15) * mm});
            skLineSegment(sketch, "E380", {"start": v(-490.48, -385.15) * mm, "end": v(-501.15, -385.15) * mm});
            skLineSegment(sketch, "E381", {"start": v(-501.15, -385.15) * mm, "end": v(-501.15, -388.15) * mm});
            skLineSegment(sketch, "E382", {"start": v(-501.15, -388.15) * mm, "end": v(-511.9, -388.15) * mm});
            skLineSegment(sketch, "E383", {"start": v(-511.9, -388.15) * mm, "end": v(-511.9, -376.28) * mm});
            skLineSegment(sketch, "E384", {"start": v(-511.9, -376.28) * mm, "end": v(-508.9, -376.28) * mm});
            skLineSegment(sketch, "E385", {"start": v(-508.9, -376.28) * mm, "end": v(-508.9, -365.61) * mm});
            skLineSegment(sketch, "E386", {"start": v(-508.9, -365.61) * mm, "end": v(-511.9, -365.61) * mm});
            skLineSegment(sketch, "E387", {"start": v(-511.9, -365.61) * mm, "end": v(-511.9, -353.75) * mm});
            skLineSegment(sketch, "E388", {"start": v(-511.9, -353.75) * mm, "end": v(-508.9, -353.75) * mm});
            skLineSegment(sketch, "E389", {"start": v(-508.9, -353.75) * mm, "end": v(-508.9, -343.08) * mm});
            skLineSegment(sketch, "E390", {"start": v(-508.9, -343.08) * mm, "end": v(-511.9, -343.08) * mm});
            skLineSegment(sketch, "E391", {"start": v(-511.9, -343.08) * mm, "end": v(-511.9, -331.22) * mm});
            skLineSegment(sketch, "E392", {"start": v(-511.9, -331.22) * mm, "end": v(-508.9, -331.22) * mm});
            skLineSegment(sketch, "E393", {"start": v(-508.9, -331.22) * mm, "end": v(-508.9, -320.55) * mm});
            skLineSegment(sketch, "E394", {"start": v(-508.9, -320.55) * mm, "end": v(-511.9, -320.55) * mm});
            skLineSegment(sketch, "E395", {"start": v(-511.9, -320.55) * mm, "end": v(-511.9, -308.68) * mm});
            skLineSegment(sketch, "E396", {"start": v(-511.9, -308.68) * mm, "end": v(-508.9, -308.68) * mm});
            skLineSegment(sketch, "E397", {"start": v(-508.9, -308.68) * mm, "end": v(-508.9, -298.01) * mm});
            skLineSegment(sketch, "E398", {"start": v(-508.9, -298.01) * mm, "end": v(-511.9, -298.01) * mm});
            skLineSegment(sketch, "E399", {"start": v(-511.9, -298.01) * mm, "end": v(-511.9, -286.15) * mm});
            skLineSegment(sketch, "E400", {"start": v(-511.9, -286.15) * mm, "end": v(-508.9, -286.15) * mm});
            skLineSegment(sketch, "E401", {"start": v(-508.9, -286.15) * mm, "end": v(-508.9, -275.48) * mm});
            skLineSegment(sketch, "E402", {"start": v(-508.9, -275.48) * mm, "end": v(-511.9, -275.48) * mm});
            skLineSegment(sketch, "E403", {"start": v(-511.9, -275.48) * mm, "end": v(-511.9, -263.61) * mm});
            skLineSegment(sketch, "E404", {"start": v(-511.9, -263.61) * mm, "end": v(-508.9, -263.61) * mm});
            skLineSegment(sketch, "E405", {"start": v(-508.9, -263.61) * mm, "end": v(-508.9, -252.95) * mm});
            skLineSegment(sketch, "E406", {"start": v(-508.9, -252.95) * mm, "end": v(-511.9, -252.95) * mm});
            skLineSegment(sketch, "E407", {"start": v(-511.9, -252.95) * mm, "end": v(-511.9, -241.08) * mm});
            skLineSegment(sketch, "E408", {"start": v(-511.9, -241.08) * mm, "end": v(-508.9, -241.08) * mm});
            skLineSegment(sketch, "E409", {"start": v(-508.9, -241.08) * mm, "end": v(-508.9, -230.41) * mm});
            skLineSegment(sketch, "E410", {"start": v(-508.9, -230.41) * mm, "end": v(-511.9, -230.41) * mm});
            skLineSegment(sketch, "E411", {"start": v(-511.9, -230.41) * mm, "end": v(-511.9, -218.55) * mm});
            skLineSegment(sketch, "E412", {"start": v(-511.9, -218.55) * mm, "end": v(-508.9, -218.55) * mm});
            skLineSegment(sketch, "E413", {"start": v(-508.9, -218.55) * mm, "end": v(-508.9, -207.88) * mm});
            skLineSegment(sketch, "E414", {"start": v(-508.9, -207.88) * mm, "end": v(-511.9, -207.88) * mm});
            skLineSegment(sketch, "E415", {"start": v(-511.9, -207.88) * mm, "end": v(-511.9, -196.01) * mm});
            skLineSegment(sketch, "E416", {"start": v(-511.9, -196.01) * mm, "end": v(-508.9, -196.01) * mm});
            skLineSegment(sketch, "E417", {"start": v(-508.9, -196.01) * mm, "end": v(-508.9, -185.35) * mm});
            skLineSegment(sketch, "E418", {"start": v(-508.9, -185.35) * mm, "end": v(-511.9, -185.35) * mm});
            skLineSegment(sketch, "E419", {"start": v(-511.9, -185.35) * mm, "end": v(-511.9, -173.48) * mm});
            skLineSegment(sketch, "E420", {"start": v(-511.9, -173.48) * mm, "end": v(-508.9, -173.48) * mm});
            skLineSegment(sketch, "E421", {"start": v(-508.9, -173.48) * mm, "end": v(-508.9, -162.81) * mm});
            skLineSegment(sketch, "E422", {"start": v(-508.9, -162.81) * mm, "end": v(-511.9, -162.81) * mm});
            skLineSegment(sketch, "E423", {"start": v(-511.9, -162.81) * mm, "end": v(-511.9, -150.95) * mm});
            skLineSegment(sketch, "E424", {"start": v(-511.9, -150.95) * mm, "end": v(-508.9, -150.95) * mm});
            skLineSegment(sketch, "E425", {"start": v(-508.9, -150.95) * mm, "end": v(-508.9, -140.28) * mm});
            skLineSegment(sketch, "E426", {"start": v(-508.9, -140.28) * mm, "end": v(-511.9, -140.28) * mm});
            skLineSegment(sketch, "E427", {"start": v(-511.9, -140.28) * mm, "end": v(-511.9, -128.41) * mm});
            skLineSegment(sketch, "E428", {"start": v(-511.9, -128.41) * mm, "end": v(-508.9, -128.41) * mm});
            skLineSegment(sketch, "E429", {"start": v(-508.9, -128.41) * mm, "end": v(-508.9, -117.75) * mm});
            skLineSegment(sketch, "E430", {"start": v(-508.9, -117.75) * mm, "end": v(-511.9, -117.75) * mm});
            skLineSegment(sketch, "E431", {"start": v(-511.9, -117.75) * mm, "end": v(-511.9, -105.88) * mm});
            skLineSegment(sketch, "E432", {"start": v(-511.9, -105.88) * mm, "end": v(-508.9, -105.88) * mm});
            skLineSegment(sketch, "E433", {"start": v(-508.9, -105.88) * mm, "end": v(-508.9, -95.21) * mm});
            skLineSegment(sketch, "E434", {"start": v(-508.9, -95.21) * mm, "end": v(-511.9, -95.21) * mm});
            skLineSegment(sketch, "E435", {"start": v(-511.9, -95.21) * mm, "end": v(-511.9, -83.35) * mm});
            skLineSegment(sketch, "E436", {"start": v(-358.57, 150.71) * mm, "end": v(380.4, 150.71) * mm});
            skLineSegment(sketch, "E437", {"start": v(-433.58, 455.51) * mm, "end": v(-422.83, 455.51) * mm});
            skLineSegment(sketch, "E438", {"start": v(-422.83, 455.51) * mm, "end": v(-422.83, 452.51) * mm});
            skLineSegment(sketch, "E439", {"start": v(-422.83, 452.51) * mm, "end": v(-412.16, 452.51) * mm});
            skLineSegment(sketch, "E440", {"start": v(-412.16, 452.51) * mm, "end": v(-412.16, 455.51) * mm});
            skLineSegment(sketch, "E441", {"start": v(-412.16, 455.51) * mm, "end": v(-401.41, 455.51) * mm});
            skLineSegment(sketch, "E442", {"start": v(-401.41, 455.51) * mm, "end": v(-401.41, 452.51) * mm});
            skLineSegment(sketch, "E443", {"start": v(-401.41, 452.51) * mm, "end": v(-390.74, 452.51) * mm});
            skLineSegment(sketch, "E444", {"start": v(-390.74, 452.51) * mm, "end": v(-390.74, 455.51) * mm});
            skLineSegment(sketch, "E445", {"start": v(-390.74, 455.51) * mm, "end": v(-380, 455.51) * mm});
            skLineSegment(sketch, "E446", {"start": v(-380, 455.51) * mm, "end": v(-380, 452.51) * mm});
            skLineSegment(sketch, "E447", {"start": v(-380, 452.51) * mm, "end": v(-369.32, 452.51) * mm});
            skLineSegment(sketch, "E448", {"start": v(-369.32, 452.51) * mm, "end": v(-369.32, 455.51) * mm});
            skLineSegment(sketch, "E449", {"start": v(-369.32, 455.51) * mm, "end": v(-358.57, 455.51) * mm});
            skLineSegment(sketch, "E450", {"start": v(380.4, 455.51) * mm, "end": v(391.15, 455.51) * mm});
            skLineSegment(sketch, "E451", {"start": v(391.15, 455.51) * mm, "end": v(391.15, 452.51) * mm});
            skLineSegment(sketch, "E452", {"start": v(391.15, 452.51) * mm, "end": v(401.82, 452.51) * mm});
            skLineSegment(sketch, "E453", {"start": v(401.82, 452.51) * mm, "end": v(401.82, 455.51) * mm});
            skLineSegment(sketch, "E454", {"start": v(401.82, 455.51) * mm, "end": v(412.57, 455.51) * mm});
            skLineSegment(sketch, "E455", {"start": v(412.57, 455.51) * mm, "end": v(412.57, 452.51) * mm});
            skLineSegment(sketch, "E456", {"start": v(412.57, 452.51) * mm, "end": v(423.24, 452.51) * mm});
            skLineSegment(sketch, "E457", {"start": v(423.24, 452.51) * mm, "end": v(423.24, 455.51) * mm});
            skLineSegment(sketch, "E458", {"start": v(423.24, 455.51) * mm, "end": v(434, 455.51) * mm});
            skLineSegment(sketch, "E459", {"start": v(434, 455.51) * mm, "end": v(434, 452.51) * mm});
            skLineSegment(sketch, "E460", {"start": v(434, 452.51) * mm, "end": v(444.66, 452.51) * mm});
            skLineSegment(sketch, "E461", {"start": v(444.66, 452.51) * mm, "end": v(444.66, 455.51) * mm});
            skLineSegment(sketch, "E462", {"start": v(444.66, 455.51) * mm, "end": v(455.42, 455.51) * mm});
            skLineSegment(sketch, "E463", {"start": v(455.42, 455.51) * mm, "end": v(455.42, 443.65) * mm});
            skLineSegment(sketch, "E464", {"start": v(455.42, 443.65) * mm, "end": v(452.42, 443.65) * mm});
            skLineSegment(sketch, "E465", {"start": v(452.42, 443.65) * mm, "end": v(452.42, 432.98) * mm});
            skLineSegment(sketch, "E466", {"start": v(452.42, 432.98) * mm, "end": v(455.42, 432.98) * mm});
            skLineSegment(sketch, "E467", {"start": v(455.42, 432.98) * mm, "end": v(455.42, 421.11) * mm});
            skLineSegment(sketch, "E468", {"start": v(455.42, 421.11) * mm, "end": v(452.42, 421.11) * mm});
            skLineSegment(sketch, "E469", {"start": v(452.42, 421.11) * mm, "end": v(452.42, 410.45) * mm});
            skLineSegment(sketch, "E470", {"start": v(452.42, 410.45) * mm, "end": v(455.42, 410.45) * mm});
            skLineSegment(sketch, "E471", {"start": v(455.42, 410.45) * mm, "end": v(455.42, 398.58) * mm});
            skLineSegment(sketch, "E472", {"start": v(455.42, 398.58) * mm, "end": v(452.42, 398.58) * mm});
            skLineSegment(sketch, "E473", {"start": v(452.42, 398.58) * mm, "end": v(452.42, 387.91) * mm});
            skLineSegment(sketch, "E474", {"start": v(452.42, 387.91) * mm, "end": v(455.42, 387.91) * mm});
            skLineSegment(sketch, "E475", {"start": v(455.42, 218.31) * mm, "end": v(452.42, 218.31) * mm});
            skLineSegment(sketch, "E476", {"start": v(452.42, 218.31) * mm, "end": v(452.42, 207.64) * mm});
            skLineSegment(sketch, "E477", {"start": v(452.42, 207.64) * mm, "end": v(455.42, 207.64) * mm});
            skLineSegment(sketch, "E478", {"start": v(455.42, 207.64) * mm, "end": v(455.42, 195.78) * mm});
            skLineSegment(sketch, "E479", {"start": v(455.42, 195.78) * mm, "end": v(452.42, 195.78) * mm});
            skLineSegment(sketch, "E480", {"start": v(452.42, 195.78) * mm, "end": v(452.42, 185.11) * mm});
            skLineSegment(sketch, "E481", {"start": v(452.42, 185.11) * mm, "end": v(455.42, 185.11) * mm});
            skLineSegment(sketch, "E482", {"start": v(455.42, 185.11) * mm, "end": v(455.42, 173.25) * mm});
            skLineSegment(sketch, "E483", {"start": v(455.42, 173.25) * mm, "end": v(452.42, 173.25) * mm});
            skLineSegment(sketch, "E484", {"start": v(452.42, 173.25) * mm, "end": v(452.42, 162.58) * mm});
            skLineSegment(sketch, "E485", {"start": v(452.42, 162.58) * mm, "end": v(455.42, 162.58) * mm});
            skLineSegment(sketch, "E486", {"start": v(455.42, 162.58) * mm, "end": v(455.42, 150.71) * mm});
            skLineSegment(sketch, "E487", {"start": v(455.42, 150.71) * mm, "end": v(444.66, 150.71) * mm});
            skLineSegment(sketch, "E488", {"start": v(444.66, 150.71) * mm, "end": v(444.66, 153.7) * mm});
            skLineSegment(sketch, "E489", {"start": v(444.66, 153.7) * mm, "end": v(434, 153.7) * mm});
            skLineSegment(sketch, "E490", {"start": v(434, 153.7) * mm, "end": v(434, 150.71) * mm});
            skLineSegment(sketch, "E491", {"start": v(434, 150.71) * mm, "end": v(423.24, 150.71) * mm});
            skLineSegment(sketch, "E492", {"start": v(423.24, 150.71) * mm, "end": v(423.24, 153.7) * mm});
            skLineSegment(sketch, "E493", {"start": v(423.24, 153.7) * mm, "end": v(412.57, 153.7) * mm});
            skLineSegment(sketch, "E494", {"start": v(412.57, 153.7) * mm, "end": v(412.57, 150.71) * mm});
            skLineSegment(sketch, "E495", {"start": v(412.57, 150.71) * mm, "end": v(401.82, 150.71) * mm});
            skLineSegment(sketch, "E496", {"start": v(401.82, 150.71) * mm, "end": v(401.82, 153.7) * mm});
            skLineSegment(sketch, "E497", {"start": v(401.82, 153.7) * mm, "end": v(391.15, 153.7) * mm});
            skLineSegment(sketch, "E498", {"start": v(391.15, 153.7) * mm, "end": v(391.15, 150.71) * mm});
            skLineSegment(sketch, "E499", {"start": v(391.15, 150.71) * mm, "end": v(380.4, 150.71) * mm});
            skLineSegment(sketch, "E500", {"start": v(-358.57, 150.71) * mm, "end": v(-369.32, 150.71) * mm});
            skLineSegment(sketch, "E501", {"start": v(-369.32, 150.71) * mm, "end": v(-369.32, 153.7) * mm});
            skLineSegment(sketch, "E502", {"start": v(-369.32, 153.7) * mm, "end": v(-380, 153.7) * mm});
            skLineSegment(sketch, "E503", {"start": v(-380, 153.7) * mm, "end": v(-380, 150.71) * mm});
            skLineSegment(sketch, "E504", {"start": v(-380, 150.71) * mm, "end": v(-390.74, 150.71) * mm});
            skLineSegment(sketch, "E505", {"start": v(-390.74, 150.71) * mm, "end": v(-390.74, 153.7) * mm});
            skLineSegment(sketch, "E506", {"start": v(-390.74, 153.7) * mm, "end": v(-401.41, 153.7) * mm});
            skLineSegment(sketch, "E507", {"start": v(-401.41, 153.7) * mm, "end": v(-401.41, 150.71) * mm});
            skLineSegment(sketch, "E508", {"start": v(-401.41, 150.71) * mm, "end": v(-412.16, 150.71) * mm});
            skLineSegment(sketch, "E509", {"start": v(-412.16, 150.71) * mm, "end": v(-412.16, 153.7) * mm});
            skLineSegment(sketch, "E510", {"start": v(-412.16, 153.7) * mm, "end": v(-422.83, 153.7) * mm});
            skLineSegment(sketch, "E511", {"start": v(-422.83, 153.7) * mm, "end": v(-422.83, 150.71) * mm});
            skLineSegment(sketch, "E512", {"start": v(-422.83, 150.71) * mm, "end": v(-433.58, 150.71) * mm});
            skLineSegment(sketch, "E513", {"start": v(-433.58, 150.71) * mm, "end": v(-433.58, 162.58) * mm});
            skLineSegment(sketch, "E514", {"start": v(-433.58, 162.58) * mm, "end": v(-430.59, 162.58) * mm});
            skLineSegment(sketch, "E515", {"start": v(-430.59, 162.58) * mm, "end": v(-430.59, 173.25) * mm});
            skLineSegment(sketch, "E516", {"start": v(-430.59, 173.25) * mm, "end": v(-433.58, 173.25) * mm});
            skLineSegment(sketch, "E517", {"start": v(-433.58, 173.25) * mm, "end": v(-433.58, 185.11) * mm});
            skLineSegment(sketch, "E518", {"start": v(-433.58, 185.11) * mm, "end": v(-430.59, 185.11) * mm});
            skLineSegment(sketch, "E519", {"start": v(-430.59, 185.11) * mm, "end": v(-430.59, 195.78) * mm});
            skLineSegment(sketch, "E520", {"start": v(-430.59, 195.78) * mm, "end": v(-433.58, 195.78) * mm});
            skLineSegment(sketch, "E521", {"start": v(-433.58, 195.78) * mm, "end": v(-433.58, 207.64) * mm});
            skLineSegment(sketch, "E522", {"start": v(-433.58, 207.64) * mm, "end": v(-430.59, 207.64) * mm});
            skLineSegment(sketch, "E523", {"start": v(-430.59, 207.64) * mm, "end": v(-430.59, 218.31) * mm});
            skLineSegment(sketch, "E524", {"start": v(-430.59, 218.31) * mm, "end": v(-433.58, 218.31) * mm});
            skLineSegment(sketch, "E525", {"start": v(-433.58, 387.91) * mm, "end": v(-430.59, 387.91) * mm});
            skLineSegment(sketch, "E526", {"start": v(-430.59, 387.91) * mm, "end": v(-430.59, 398.58) * mm});
            skLineSegment(sketch, "E527", {"start": v(-430.59, 398.58) * mm, "end": v(-433.58, 398.58) * mm});
            skLineSegment(sketch, "E528", {"start": v(-433.58, 398.58) * mm, "end": v(-433.58, 410.45) * mm});
            skLineSegment(sketch, "E529", {"start": v(-433.58, 410.45) * mm, "end": v(-430.59, 410.45) * mm});
            skLineSegment(sketch, "E530", {"start": v(-430.59, 410.45) * mm, "end": v(-430.59, 421.11) * mm});
            skLineSegment(sketch, "E531", {"start": v(-430.59, 421.11) * mm, "end": v(-433.58, 421.11) * mm});
            skLineSegment(sketch, "E532", {"start": v(-433.58, 421.11) * mm, "end": v(-433.58, 432.98) * mm});
            skLineSegment(sketch, "E533", {"start": v(-433.58, 432.98) * mm, "end": v(-430.59, 432.98) * mm});
            skLineSegment(sketch, "E534", {"start": v(-430.59, 432.98) * mm, "end": v(-430.59, 443.65) * mm});
            skLineSegment(sketch, "E535", {"start": v(-430.59, 443.65) * mm, "end": v(-433.58, 443.65) * mm});
            skLineSegment(sketch, "E536", {"start": v(-433.58, 443.65) * mm, "end": v(-433.58, 455.51) * mm});
            skLineSegment(sketch, "E537", {"start": v(455.42, 387.91) * mm, "end": v(455.42, 218.31) * mm});
            skLineSegment(sketch, "E538", {"start": v(-433.58, 218.31) * mm, "end": v(-433.58, 387.91) * mm});
            skLineSegment(sketch, "E539", {"start": v(-449.28, 216.64) * mm, "end": v(-449.28, 386.24) * mm});
            skLineSegment(sketch, "E540", {"start": v(-449.28, 152.04) * mm, "end": v(-463.18, 152.04) * mm});
            skLineSegment(sketch, "E541", {"start": v(-463.18, 152.04) * mm, "end": v(-463.18, 149.04) * mm});
            skLineSegment(sketch, "E542", {"start": v(-463.18, 149.04) * mm, "end": v(-473.84, 149.04) * mm});
            skLineSegment(sketch, "E543", {"start": v(-473.84, 149.04) * mm, "end": v(-473.84, 152.04) * mm});
            skLineSegment(sketch, "E544", {"start": v(-473.84, 152.04) * mm, "end": v(-487.74, 152.04) * mm});
            skLineSegment(sketch, "E545", {"start": v(-487.74, 152.04) * mm, "end": v(-487.74, 160.9) * mm});
            skLineSegment(sketch, "E546", {"start": v(-487.74, 160.9) * mm, "end": v(-490.73, 160.9) * mm});
            skLineSegment(sketch, "E547", {"start": v(-490.73, 171.58) * mm, "end": v(-487.74, 171.58) * mm});
            skLineSegment(sketch, "E548", {"start": v(-487.74, 171.58) * mm, "end": v(-487.74, 183.44) * mm});
            skLineSegment(sketch, "E549", {"start": v(-487.74, 183.44) * mm, "end": v(-490.73, 183.44) * mm});
            skLineSegment(sketch, "E550", {"start": v(-490.73, 194.1) * mm, "end": v(-487.74, 194.1) * mm});
            skLineSegment(sketch, "E551", {"start": v(-487.74, 194.1) * mm, "end": v(-487.74, 205.98) * mm});
            skLineSegment(sketch, "E552", {"start": v(-487.74, 205.98) * mm, "end": v(-490.73, 205.98) * mm});
            skLineSegment(sketch, "E553", {"start": v(-490.73, 216.64) * mm, "end": v(-487.74, 216.64) * mm});
            skLineSegment(sketch, "E554", {"start": v(-487.74, 216.64) * mm, "end": v(-487.74, 228.5) * mm});
            skLineSegment(sketch, "E555", {"start": v(-487.74, 228.5) * mm, "end": v(-490.73, 228.5) * mm});
            skLineSegment(sketch, "E556", {"start": v(-490.73, 239.18) * mm, "end": v(-487.74, 239.18) * mm});
            skLineSegment(sketch, "E557", {"start": v(-487.74, 239.18) * mm, "end": v(-487.74, 251.04) * mm});
            skLineSegment(sketch, "E558", {"start": v(-487.74, 251.04) * mm, "end": v(-490.73, 251.04) * mm});
            skLineSegment(sketch, "E559", {"start": v(-490.73, 261.71) * mm, "end": v(-487.74, 261.71) * mm});
            skLineSegment(sketch, "E560", {"start": v(-487.74, 261.71) * mm, "end": v(-487.74, 273.58) * mm});
            skLineSegment(sketch, "E561", {"start": v(-487.74, 273.58) * mm, "end": v(-490.73, 273.58) * mm});
            skLineSegment(sketch, "E562", {"start": v(-490.73, 284.24) * mm, "end": v(-487.74, 284.24) * mm});
            skLineSegment(sketch, "E563", {"start": v(-487.74, 284.24) * mm, "end": v(-487.74, 296.1) * mm});
            skLineSegment(sketch, "E564", {"start": v(-487.74, 296.1) * mm, "end": v(-490.73, 296.1) * mm});
            skLineSegment(sketch, "E565", {"start": v(-490.73, 306.78) * mm, "end": v(-487.74, 306.78) * mm});
            skLineSegment(sketch, "E566", {"start": v(-487.74, 306.78) * mm, "end": v(-487.74, 318.64) * mm});
            skLineSegment(sketch, "E567", {"start": v(-487.74, 318.64) * mm, "end": v(-490.73, 318.64) * mm});
            skLineSegment(sketch, "E568", {"start": v(-490.73, 329.31) * mm, "end": v(-487.74, 329.31) * mm});
            skLineSegment(sketch, "E569", {"start": v(-487.74, 329.31) * mm, "end": v(-487.74, 341.18) * mm});
            skLineSegment(sketch, "E570", {"start": v(-487.74, 341.18) * mm, "end": v(-490.73, 341.18) * mm});
            skLineSegment(sketch, "E571", {"start": v(-490.73, 351.84) * mm, "end": v(-487.74, 351.84) * mm});
            skLineSegment(sketch, "E572", {"start": v(-487.74, 351.84) * mm, "end": v(-487.74, 363.7) * mm});
            skLineSegment(sketch, "E573", {"start": v(-487.74, 363.7) * mm, "end": v(-490.73, 363.7) * mm});
            skLineSegment(sketch, "E574", {"start": v(-490.73, 374.38) * mm, "end": v(-487.74, 374.38) * mm});
            skLineSegment(sketch, "E575", {"start": v(-487.74, 374.38) * mm, "end": v(-487.74, 386.24) * mm});
            skLineSegment(sketch, "E576", {"start": v(-487.74, 386.24) * mm, "end": v(-490.73, 386.24) * mm});
            skLineSegment(sketch, "E577", {"start": v(-490.73, 396.91) * mm, "end": v(-487.74, 396.91) * mm});
            skLineSegment(sketch, "E578", {"start": v(-487.74, 396.91) * mm, "end": v(-487.74, 408.78) * mm});
            skLineSegment(sketch, "E579", {"start": v(-487.74, 408.78) * mm, "end": v(-490.73, 408.78) * mm});
            skLineSegment(sketch, "E580", {"start": v(-490.73, 419.44) * mm, "end": v(-487.74, 419.44) * mm});
            skLineSegment(sketch, "E581", {"start": v(-487.74, 419.44) * mm, "end": v(-487.74, 431.3) * mm});
            skLineSegment(sketch, "E582", {"start": v(-487.74, 431.3) * mm, "end": v(-490.73, 431.3) * mm});
            skLineSegment(sketch, "E583", {"start": v(-490.73, 441.98) * mm, "end": v(-487.74, 441.98) * mm});
            skLineSegment(sketch, "E584", {"start": v(-487.74, 441.98) * mm, "end": v(-487.74, 450.85) * mm});
            skLineSegment(sketch, "E585", {"start": v(-487.74, 450.85) * mm, "end": v(-473.84, 450.85) * mm});
            skLineSegment(sketch, "E586", {"start": v(-473.84, 450.85) * mm, "end": v(-473.84, 453.84) * mm});
            skLineSegment(sketch, "E587", {"start": v(-473.84, 453.84) * mm, "end": v(-463.18, 453.84) * mm});
            skLineSegment(sketch, "E588", {"start": v(-463.18, 453.84) * mm, "end": v(-463.18, 450.85) * mm});
            skLineSegment(sketch, "E589", {"start": v(-463.18, 450.85) * mm, "end": v(-449.28, 450.85) * mm});
            skLineSegment(sketch, "E590", {"start": v(-449.28, 450.85) * mm, "end": v(-449.28, 441.98) * mm});
            skLineSegment(sketch, "E591", {"start": v(-449.28, 441.98) * mm, "end": v(-446.28, 441.98) * mm});
            skLineSegment(sketch, "E592", {"start": v(-446.28, 441.98) * mm, "end": v(-446.28, 431.3) * mm});
            skLineSegment(sketch, "E593", {"start": v(-446.28, 431.3) * mm, "end": v(-449.28, 431.3) * mm});
            skLineSegment(sketch, "E594", {"start": v(-449.28, 431.3) * mm, "end": v(-449.28, 419.44) * mm});
            skLineSegment(sketch, "E595", {"start": v(-449.28, 419.44) * mm, "end": v(-446.28, 419.44) * mm});
            skLineSegment(sketch, "E596", {"start": v(-446.28, 419.44) * mm, "end": v(-446.28, 408.78) * mm});
            skLineSegment(sketch, "E597", {"start": v(-446.28, 408.78) * mm, "end": v(-449.28, 408.78) * mm});
            skLineSegment(sketch, "E598", {"start": v(-449.28, 408.78) * mm, "end": v(-449.28, 396.91) * mm});
            skLineSegment(sketch, "E599", {"start": v(-449.28, 396.91) * mm, "end": v(-446.28, 396.91) * mm});
            skLineSegment(sketch, "E600", {"start": v(-446.28, 396.91) * mm, "end": v(-446.28, 386.24) * mm});
            skLineSegment(sketch, "E601", {"start": v(-446.28, 386.24) * mm, "end": v(-449.28, 386.24) * mm});
            skLineSegment(sketch, "E602", {"start": v(-449.28, 216.64) * mm, "end": v(-446.28, 216.64) * mm});
            skLineSegment(sketch, "E603", {"start": v(-446.28, 216.64) * mm, "end": v(-446.28, 205.98) * mm});
            skLineSegment(sketch, "E604", {"start": v(-446.28, 205.98) * mm, "end": v(-449.28, 205.98) * mm});
            skLineSegment(sketch, "E605", {"start": v(-449.28, 205.98) * mm, "end": v(-449.28, 194.1) * mm});
            skLineSegment(sketch, "E606", {"start": v(-449.28, 194.1) * mm, "end": v(-446.28, 194.1) * mm});
            skLineSegment(sketch, "E607", {"start": v(-446.28, 194.1) * mm, "end": v(-446.28, 183.44) * mm});
            skLineSegment(sketch, "E608", {"start": v(-446.28, 183.44) * mm, "end": v(-449.28, 183.44) * mm});
            skLineSegment(sketch, "E609", {"start": v(-449.28, 183.44) * mm, "end": v(-449.28, 171.58) * mm});
            skLineSegment(sketch, "E610", {"start": v(-449.28, 171.58) * mm, "end": v(-446.28, 171.58) * mm});
            skLineSegment(sketch, "E611", {"start": v(-446.28, 171.58) * mm, "end": v(-446.28, 160.9) * mm});
            skLineSegment(sketch, "E612", {"start": v(-446.28, 160.9) * mm, "end": v(-449.28, 160.9) * mm});
            skLineSegment(sketch, "E613", {"start": v(-449.28, 160.9) * mm, "end": v(-449.28, 152.04) * mm});
            skCircle(sketch, "E614", {"center": v(231.67, 162.57) * mm, "radius": 2.18 * mm});
            skCircle(sketch, "E615", {"center": v(-209.84, 162.57) * mm, "radius": 2.18 * mm});
            skCircle(sketch, "E616", {"center": v(231.67, 443.65) * mm, "radius": 2.18 * mm});
            skCircle(sketch, "E617", {"center": v(-209.84, 443.65) * mm, "radius": 2.18 * mm});
            skCircle(sketch, "E618", {"center": v(-422.83, 303.11) * mm, "radius": 2.18 * mm});
            skCircle(sketch, "E619", {"center": v(-456.23, 301.44) * mm, "radius": 2.18 * mm});
            skLineSegment(sketch, "E620", {"start": v(-473.59, 412.68) * mm, "end": v(-463.1, 412.68) * mm});
            skLineSegment(sketch, "E621", {"start": v(-463.1, 412.68) * mm, "end": v(-463.1, 438.08) * mm});
            skLineSegment(sketch, "E622", {"start": v(-463.1, 438.08) * mm, "end": v(-473.59, 438.08) * mm});
            skLineSegment(sketch, "E623", {"start": v(-473.59, 438.08) * mm, "end": v(-473.59, 412.68) * mm});
            skCircle(sketch, "E624", {"center": v(-468.5, 377.64) * mm, "radius": 2.08 * mm});
            skCircle(sketch, "E625", {"center": v(-468.5, 225.24) * mm, "radius": 2.08 * mm});
            skLineSegment(sketch, "E626", {"start": v(-490.73, 171.58) * mm, "end": v(-490.73, 183.44) * mm});
            skLineSegment(sketch, "E627", {"start": v(-490.73, 194.1) * mm, "end": v(-490.73, 205.98) * mm});
            skLineSegment(sketch, "E628", {"start": v(-490.73, 216.64) * mm, "end": v(-490.73, 228.5) * mm});
            skLineSegment(sketch, "E629", {"start": v(-490.73, 239.18) * mm, "end": v(-490.73, 251.04) * mm});
            skLineSegment(sketch, "E630", {"start": v(-490.73, 261.71) * mm, "end": v(-490.73, 273.58) * mm});
            skLineSegment(sketch, "E631", {"start": v(-490.73, 284.24) * mm, "end": v(-490.73, 296.1) * mm});
            skLineSegment(sketch, "E632", {"start": v(-490.73, 306.78) * mm, "end": v(-490.73, 318.64) * mm});
            skLineSegment(sketch, "E633", {"start": v(-490.73, 351.84) * mm, "end": v(-490.73, 363.7) * mm});
            skLineSegment(sketch, "E634", {"start": v(-490.73, 374.38) * mm, "end": v(-490.73, 386.24) * mm});
            skLineSegment(sketch, "E635", {"start": v(-490.73, 396.91) * mm, "end": v(-490.73, 408.78) * mm});
            skLineSegment(sketch, "E636", {"start": v(-490.73, 419.44) * mm, "end": v(-490.73, 431.3) * mm});
            skLineSegment(sketch, "E637", {"start": v(-490.73, 329.31) * mm, "end": v(-490.73, 341.18) * mm});
            skCircle(sketch, "E638", {"center": v(444.64, 303.1) * mm, "radius": 2.18 * mm});
            skLineSegment(sketch, "E639", {"start": v(-458.22, 25.42) * mm, "end": v(302.25, 25.42) * mm});
            skLineSegment(sketch, "E640", {"start": v(-522.48, 25.42) * mm, "end": v(-511.73, 25.42) * mm});
            skLineSegment(sketch, "E641", {"start": v(-511.73, 25.42) * mm, "end": v(-511.73, 28.41) * mm});
            skLineSegment(sketch, "E642", {"start": v(-511.73, 28.41) * mm, "end": v(-501.06, 28.41) * mm});
            skLineSegment(sketch, "E643", {"start": v(-501.06, 28.41) * mm, "end": v(-501.06, 25.42) * mm});
            skLineSegment(sketch, "E644", {"start": v(-501.06, 25.42) * mm, "end": v(-490.31, 25.42) * mm});
            skLineSegment(sketch, "E645", {"start": v(-490.31, 25.42) * mm, "end": v(-490.31, 28.41) * mm});
            skLineSegment(sketch, "E646", {"start": v(-490.31, 28.41) * mm, "end": v(-479.64, 28.41) * mm});
            skLineSegment(sketch, "E647", {"start": v(-479.64, 28.41) * mm, "end": v(-479.64, 25.42) * mm});
            skLineSegment(sketch, "E648", {"start": v(-479.64, 25.42) * mm, "end": v(-468.9, 25.42) * mm});
            skLineSegment(sketch, "E649", {"start": v(-468.9, 25.42) * mm, "end": v(-468.9, 28.41) * mm});
            skLineSegment(sketch, "E650", {"start": v(-468.9, 28.41) * mm, "end": v(-458.22, 28.41) * mm});
            skLineSegment(sketch, "E651", {"start": v(-458.22, 28.41) * mm, "end": v(-458.22, 25.42) * mm});
            skLineSegment(sketch, "E652", {"start": v(302.25, 25.42) * mm, "end": v(302.25, 28.41) * mm});
            skLineSegment(sketch, "E653", {"start": v(302.25, 28.41) * mm, "end": v(312.92, 28.41) * mm});
            skLineSegment(sketch, "E654", {"start": v(312.92, 28.41) * mm, "end": v(312.92, 25.42) * mm});
            skLineSegment(sketch, "E655", {"start": v(312.92, 25.42) * mm, "end": v(323.67, 25.42) * mm});
            skLineSegment(sketch, "E656", {"start": v(323.67, 25.42) * mm, "end": v(323.67, 28.41) * mm});
            skLineSegment(sketch, "E657", {"start": v(323.67, 28.41) * mm, "end": v(334.34, 28.41) * mm});
            skLineSegment(sketch, "E658", {"start": v(334.34, 28.41) * mm, "end": v(334.34, 25.42) * mm});
            skLineSegment(sketch, "E659", {"start": v(334.34, 25.42) * mm, "end": v(345.1, 25.42) * mm});
            skLineSegment(sketch, "E660", {"start": v(345.1, 25.42) * mm, "end": v(345.1, 28.41) * mm});
            skLineSegment(sketch, "E661", {"start": v(345.1, 28.41) * mm, "end": v(355.76, 28.41) * mm});
            skLineSegment(sketch, "E662", {"start": v(355.76, 28.41) * mm, "end": v(355.76, 25.42) * mm});
            skLineSegment(sketch, "E663", {"start": v(355.76, 25.42) * mm, "end": v(366.52, 25.42) * mm});
            skLineSegment(sketch, "E664", {"start": v(366.52, 25.42) * mm, "end": v(366.52, 11.52) * mm});
            skLineSegment(sketch, "E665", {"start": v(366.52, 11.52) * mm, "end": v(363.52, 11.52) * mm});
            skLineSegment(sketch, "E666", {"start": v(363.52, 11.52) * mm, "end": v(363.52, 0.86) * mm});
            skLineSegment(sketch, "E667", {"start": v(363.52, 0.86) * mm, "end": v(366.52, 0.86) * mm});
            skLineSegment(sketch, "E668", {"start": v(366.52, 0.86) * mm, "end": v(366.52, -13.04) * mm});
            skLineSegment(sketch, "E669", {"start": v(366.52, -13.04) * mm, "end": v(355.76, -13.04) * mm});
            skLineSegment(sketch, "E670", {"start": v(355.76, -13.04) * mm, "end": v(355.76, -16.04) * mm});
            skLineSegment(sketch, "E671", {"start": v(345.1, -16.04) * mm, "end": v(345.1, -13.04) * mm});
            skLineSegment(sketch, "E672", {"start": v(345.1, -13.04) * mm, "end": v(334.34, -13.04) * mm});
            skLineSegment(sketch, "E673", {"start": v(334.34, -13.04) * mm, "end": v(334.34, -16.04) * mm});
            skLineSegment(sketch, "E674", {"start": v(323.67, -16.04) * mm, "end": v(323.67, -13.04) * mm});
            skLineSegment(sketch, "E675", {"start": v(323.67, -13.04) * mm, "end": v(312.92, -13.04) * mm});
            skLineSegment(sketch, "E676", {"start": v(312.92, -13.04) * mm, "end": v(312.92, -16.04) * mm});
            skLineSegment(sketch, "E677", {"start": v(302.25, -16.04) * mm, "end": v(302.25, -13.04) * mm});
            skLineSegment(sketch, "E678", {"start": v(302.25, -13.04) * mm, "end": v(291.5, -13.04) * mm});
            skLineSegment(sketch, "E679", {"start": v(291.5, -13.04) * mm, "end": v(291.5, -16.04) * mm});
            skLineSegment(sketch, "E680", {"start": v(280.83, -16.04) * mm, "end": v(280.83, -13.04) * mm});
            skLineSegment(sketch, "E681", {"start": v(280.83, -13.04) * mm, "end": v(270.08, -13.04) * mm});
            skLineSegment(sketch, "E682", {"start": v(270.08, -13.04) * mm, "end": v(270.08, -16.04) * mm});
            skLineSegment(sketch, "E683", {"start": v(259.41, -16.04) * mm, "end": v(259.41, -13.04) * mm});
            skLineSegment(sketch, "E684", {"start": v(259.41, -13.04) * mm, "end": v(248.66, -13.04) * mm});
            skLineSegment(sketch, "E685", {"start": v(248.66, -13.04) * mm, "end": v(248.66, -16.04) * mm});
            skLineSegment(sketch, "E686", {"start": v(238, -16.04) * mm, "end": v(238, -13.04) * mm});
            skLineSegment(sketch, "E687", {"start": v(238, -13.04) * mm, "end": v(227.24, -13.04) * mm});
            skLineSegment(sketch, "E688", {"start": v(227.24, -13.04) * mm, "end": v(227.24, -16.04) * mm});
            skLineSegment(sketch, "E689", {"start": v(216.57, -16.04) * mm, "end": v(216.57, -13.04) * mm});
            skLineSegment(sketch, "E690", {"start": v(216.57, -13.04) * mm, "end": v(205.82, -13.04) * mm});
            skLineSegment(sketch, "E691", {"start": v(205.82, -13.04) * mm, "end": v(205.82, -16.04) * mm});
            skLineSegment(sketch, "E692", {"start": v(195.15, -16.04) * mm, "end": v(195.15, -13.04) * mm});
            skLineSegment(sketch, "E693", {"start": v(195.15, -13.04) * mm, "end": v(184.4, -13.04) * mm});
            skLineSegment(sketch, "E694", {"start": v(184.4, -13.04) * mm, "end": v(184.4, -16.04) * mm});
            skLineSegment(sketch, "E695", {"start": v(173.73, -16.04) * mm, "end": v(173.73, -13.04) * mm});
            skLineSegment(sketch, "E696", {"start": v(173.73, -13.04) * mm, "end": v(162.98, -13.04) * mm});
            skLineSegment(sketch, "E697", {"start": v(162.98, -13.04) * mm, "end": v(162.98, -16.04) * mm});
            skLineSegment(sketch, "E698", {"start": v(152.3, -16.04) * mm, "end": v(152.3, -13.04) * mm});
            skLineSegment(sketch, "E699", {"start": v(152.3, -13.04) * mm, "end": v(141.56, -13.04) * mm});
            skLineSegment(sketch, "E700", {"start": v(141.56, -13.04) * mm, "end": v(141.56, -16.04) * mm});
            skLineSegment(sketch, "E701", {"start": v(130.89, -16.04) * mm, "end": v(130.89, -13.04) * mm});
            skLineSegment(sketch, "E702", {"start": v(130.89, -13.04) * mm, "end": v(120.14, -13.04) * mm});
            skLineSegment(sketch, "E703", {"start": v(120.14, -13.04) * mm, "end": v(120.14, -16.04) * mm});
            skLineSegment(sketch, "E704", {"start": v(109.47, -16.04) * mm, "end": v(109.47, -13.04) * mm});
            skLineSegment(sketch, "E705", {"start": v(109.47, -13.04) * mm, "end": v(98.71, -13.04) * mm});
            skLineSegment(sketch, "E706", {"start": v(98.71, -13.04) * mm, "end": v(98.71, -16.04) * mm});
            skLineSegment(sketch, "E707", {"start": v(88.05, -16.04) * mm, "end": v(88.05, -13.04) * mm});
            skLineSegment(sketch, "E708", {"start": v(88.05, -13.04) * mm, "end": v(77.3, -13.04) * mm});
            skLineSegment(sketch, "E709", {"start": v(77.3, -13.04) * mm, "end": v(77.3, -16.04) * mm});
            skLineSegment(sketch, "E710", {"start": v(66.63, -16.04) * mm, "end": v(66.63, -13.04) * mm});
            skLineSegment(sketch, "E711", {"start": v(66.63, -13.04) * mm, "end": v(55.87, -13.04) * mm});
            skLineSegment(sketch, "E712", {"start": v(55.87, -13.04) * mm, "end": v(55.87, -16.04) * mm});
            skLineSegment(sketch, "E713", {"start": v(45.2, -16.04) * mm, "end": v(45.2, -13.04) * mm});
            skLineSegment(sketch, "E714", {"start": v(45.2, -13.04) * mm, "end": v(34.45, -13.04) * mm});
            skLineSegment(sketch, "E715", {"start": v(34.45, -13.04) * mm, "end": v(34.45, -16.04) * mm});
            skLineSegment(sketch, "E716", {"start": v(23.78, -16.04) * mm, "end": v(23.78, -13.04) * mm});
            skLineSegment(sketch, "E717", {"start": v(23.78, -13.04) * mm, "end": v(13.03, -13.04) * mm});
            skLineSegment(sketch, "E718", {"start": v(13.03, -13.04) * mm, "end": v(13.03, -16.04) * mm});
            skLineSegment(sketch, "E719", {"start": v(2.36, -16.04) * mm, "end": v(2.36, -13.04) * mm});
            skLineSegment(sketch, "E720", {"start": v(2.36, -13.04) * mm, "end": v(-8.39, -13.04) * mm});
            skLineSegment(sketch, "E721", {"start": v(-8.39, -13.04) * mm, "end": v(-8.39, -16.04) * mm});
            skLineSegment(sketch, "E722", {"start": v(-19.06, -16.04) * mm, "end": v(-19.06, -13.04) * mm});
            skLineSegment(sketch, "E723", {"start": v(-19.06, -13.04) * mm, "end": v(-29.8, -13.04) * mm});
            skLineSegment(sketch, "E724", {"start": v(-29.8, -13.04) * mm, "end": v(-29.8, -16.04) * mm});
            skLineSegment(sketch, "E725", {"start": v(-40.48, -16.04) * mm, "end": v(-40.48, -13.04) * mm});
            skLineSegment(sketch, "E726", {"start": v(-40.48, -13.04) * mm, "end": v(-51.23, -13.04) * mm});
            skLineSegment(sketch, "E727", {"start": v(-51.23, -13.04) * mm, "end": v(-51.23, -16.04) * mm});
            skLineSegment(sketch, "E728", {"start": v(-61.9, -16.04) * mm, "end": v(-61.9, -13.04) * mm});
            skLineSegment(sketch, "E729", {"start": v(-61.9, -13.04) * mm, "end": v(-72.65, -13.04) * mm});
            skLineSegment(sketch, "E730", {"start": v(-72.65, -13.04) * mm, "end": v(-72.65, -16.04) * mm});
            skLineSegment(sketch, "E731", {"start": v(-83.32, -16.04) * mm, "end": v(-83.32, -13.04) * mm});
            skLineSegment(sketch, "E732", {"start": v(-83.32, -13.04) * mm, "end": v(-94.07, -13.04) * mm});
            skLineSegment(sketch, "E733", {"start": v(-94.07, -13.04) * mm, "end": v(-94.07, -16.04) * mm});
            skLineSegment(sketch, "E734", {"start": v(-104.74, -16.04) * mm, "end": v(-104.74, -13.04) * mm});
            skLineSegment(sketch, "E735", {"start": v(-104.74, -13.04) * mm, "end": v(-115.5, -13.04) * mm});
            skLineSegment(sketch, "E736", {"start": v(-115.5, -13.04) * mm, "end": v(-115.5, -16.04) * mm});
            skLineSegment(sketch, "E737", {"start": v(-126.16, -16.04) * mm, "end": v(-126.16, -13.04) * mm});
            skLineSegment(sketch, "E738", {"start": v(-126.16, -13.04) * mm, "end": v(-136.91, -13.04) * mm});
            skLineSegment(sketch, "E739", {"start": v(-136.91, -13.04) * mm, "end": v(-136.91, -16.04) * mm});
            skLineSegment(sketch, "E740", {"start": v(-147.58, -16.04) * mm, "end": v(-147.58, -13.04) * mm});
            skLineSegment(sketch, "E741", {"start": v(-147.58, -13.04) * mm, "end": v(-158.33, -13.04) * mm});
            skLineSegment(sketch, "E742", {"start": v(-158.33, -13.04) * mm, "end": v(-158.33, -16.04) * mm});
            skLineSegment(sketch, "E743", {"start": v(-169, -16.04) * mm, "end": v(-169, -13.04) * mm});
            skLineSegment(sketch, "E744", {"start": v(-169, -13.04) * mm, "end": v(-179.75, -13.04) * mm});
            skLineSegment(sketch, "E745", {"start": v(-179.75, -13.04) * mm, "end": v(-179.75, -16.04) * mm});
            skLineSegment(sketch, "E746", {"start": v(-190.42, -16.04) * mm, "end": v(-190.42, -13.04) * mm});
            skLineSegment(sketch, "E747", {"start": v(-190.42, -13.04) * mm, "end": v(-201.17, -13.04) * mm});
            skLineSegment(sketch, "E748", {"start": v(-201.17, -13.04) * mm, "end": v(-201.17, -16.04) * mm});
            skLineSegment(sketch, "E749", {"start": v(-211.84, -16.04) * mm, "end": v(-211.84, -13.04) * mm});
            skLineSegment(sketch, "E750", {"start": v(-211.84, -13.04) * mm, "end": v(-222.6, -13.04) * mm});
            skLineSegment(sketch, "E751", {"start": v(-222.6, -13.04) * mm, "end": v(-222.6, -16.04) * mm});
            skLineSegment(sketch, "E752", {"start": v(-233.26, -16.04) * mm, "end": v(-233.26, -13.04) * mm});
            skLineSegment(sketch, "E753", {"start": v(-233.26, -13.04) * mm, "end": v(-244.02, -13.04) * mm});
            skLineSegment(sketch, "E754", {"start": v(-244.02, -13.04) * mm, "end": v(-244.02, -16.04) * mm});
            skLineSegment(sketch, "E755", {"start": v(-254.68, -16.04) * mm, "end": v(-254.68, -13.04) * mm});
            skLineSegment(sketch, "E756", {"start": v(-254.68, -13.04) * mm, "end": v(-265.44, -13.04) * mm});
            skLineSegment(sketch, "E757", {"start": v(-265.44, -13.04) * mm, "end": v(-265.44, -16.04) * mm});
            skLineSegment(sketch, "E758", {"start": v(-276.1, -16.04) * mm, "end": v(-276.1, -13.04) * mm});
            skLineSegment(sketch, "E759", {"start": v(-276.1, -13.04) * mm, "end": v(-286.86, -13.04) * mm});
            skLineSegment(sketch, "E760", {"start": v(-286.86, -13.04) * mm, "end": v(-286.86, -16.04) * mm});
            skLineSegment(sketch, "E761", {"start": v(-297.53, -16.04) * mm, "end": v(-297.53, -13.04) * mm});
            skLineSegment(sketch, "E762", {"start": v(-297.53, -13.04) * mm, "end": v(-308.28, -13.04) * mm});
            skLineSegment(sketch, "E763", {"start": v(-308.28, -13.04) * mm, "end": v(-308.28, -16.04) * mm});
            skLineSegment(sketch, "E764", {"start": v(-318.95, -16.04) * mm, "end": v(-318.95, -13.04) * mm});
            skLineSegment(sketch, "E765", {"start": v(-318.95, -13.04) * mm, "end": v(-329.7, -13.04) * mm});
            skLineSegment(sketch, "E766", {"start": v(-329.7, -13.04) * mm, "end": v(-329.7, -16.04) * mm});
            skLineSegment(sketch, "E767", {"start": v(-340.37, -16.04) * mm, "end": v(-340.37, -13.04) * mm});
            skLineSegment(sketch, "E768", {"start": v(-340.37, -13.04) * mm, "end": v(-351.12, -13.04) * mm});
            skLineSegment(sketch, "E769", {"start": v(-351.12, -13.04) * mm, "end": v(-351.12, -16.04) * mm});
            skLineSegment(sketch, "E770", {"start": v(-361.79, -16.04) * mm, "end": v(-361.79, -13.04) * mm});
            skLineSegment(sketch, "E771", {"start": v(-361.79, -13.04) * mm, "end": v(-372.54, -13.04) * mm});
            skLineSegment(sketch, "E772", {"start": v(-372.54, -13.04) * mm, "end": v(-372.54, -16.04) * mm});
            skLineSegment(sketch, "E773", {"start": v(-383.2, -16.04) * mm, "end": v(-383.2, -13.04) * mm});
            skLineSegment(sketch, "E774", {"start": v(-383.2, -13.04) * mm, "end": v(-393.96, -13.04) * mm});
            skLineSegment(sketch, "E775", {"start": v(-393.96, -13.04) * mm, "end": v(-393.96, -16.04) * mm});
            skLineSegment(sketch, "E776", {"start": v(-404.63, -16.04) * mm, "end": v(-404.63, -13.04) * mm});
            skLineSegment(sketch, "E777", {"start": v(-404.63, -13.04) * mm, "end": v(-415.38, -13.04) * mm});
            skLineSegment(sketch, "E778", {"start": v(-415.38, -13.04) * mm, "end": v(-415.38, -16.04) * mm});
            skLineSegment(sketch, "E779", {"start": v(-426.05, -16.04) * mm, "end": v(-426.05, -13.04) * mm});
            skLineSegment(sketch, "E780", {"start": v(-426.05, -13.04) * mm, "end": v(-436.8, -13.04) * mm});
            skLineSegment(sketch, "E781", {"start": v(-436.8, -13.04) * mm, "end": v(-436.8, -16.04) * mm});
            skLineSegment(sketch, "E782", {"start": v(-447.47, -16.04) * mm, "end": v(-447.47, -13.04) * mm});
            skLineSegment(sketch, "E783", {"start": v(-447.47, -13.04) * mm, "end": v(-458.22, -13.04) * mm});
            skLineSegment(sketch, "E784", {"start": v(-458.22, -13.04) * mm, "end": v(-458.22, -16.04) * mm});
            skLineSegment(sketch, "E785", {"start": v(-468.9, -16.04) * mm, "end": v(-468.9, -13.04) * mm});
            skLineSegment(sketch, "E786", {"start": v(-468.9, -13.04) * mm, "end": v(-479.64, -13.04) * mm});
            skLineSegment(sketch, "E787", {"start": v(-479.64, -13.04) * mm, "end": v(-479.64, -16.04) * mm});
            skLineSegment(sketch, "E788", {"start": v(-490.31, -16.04) * mm, "end": v(-490.31, -13.04) * mm});
            skLineSegment(sketch, "E789", {"start": v(-490.31, -13.04) * mm, "end": v(-501.06, -13.04) * mm});
            skLineSegment(sketch, "E790", {"start": v(-501.06, -13.04) * mm, "end": v(-501.06, -16.04) * mm});
            skLineSegment(sketch, "E791", {"start": v(-511.73, -16.04) * mm, "end": v(-511.73, -13.04) * mm});
            skLineSegment(sketch, "E792", {"start": v(-511.73, -13.04) * mm, "end": v(-522.48, -13.04) * mm});
            skLineSegment(sketch, "E793", {"start": v(-522.48, -13.04) * mm, "end": v(-522.48, 0.86) * mm});
            skLineSegment(sketch, "E794", {"start": v(-522.48, 0.86) * mm, "end": v(-519.49, 0.86) * mm});
            skLineSegment(sketch, "E795", {"start": v(-519.49, 0.86) * mm, "end": v(-519.49, 11.52) * mm});
            skLineSegment(sketch, "E796", {"start": v(-519.49, 11.52) * mm, "end": v(-522.48, 11.52) * mm});
            skLineSegment(sketch, "E797", {"start": v(-522.48, 11.52) * mm, "end": v(-522.48, 25.42) * mm});
            skCircle(sketch, "E798", {"center": v(142.77, 11.52) * mm, "radius": 2.18 * mm});
            skCircle(sketch, "E799", {"center": v(-298.74, 11.52) * mm, "radius": 2.18 * mm});
            skLineSegment(sketch, "E800", {"start": v(-501.06, -16.04) * mm, "end": v(-490.31, -16.04) * mm});
            skLineSegment(sketch, "E801", {"start": v(-479.64, -16.04) * mm, "end": v(-468.9, -16.04) * mm});
            skLineSegment(sketch, "E802", {"start": v(-458.22, -16.04) * mm, "end": v(-447.47, -16.04) * mm});
            skLineSegment(sketch, "E803", {"start": v(-436.8, -16.04) * mm, "end": v(-426.05, -16.04) * mm});
            skLineSegment(sketch, "E804", {"start": v(-415.38, -16.04) * mm, "end": v(-404.63, -16.04) * mm});
            skLineSegment(sketch, "E805", {"start": v(-393.96, -16.04) * mm, "end": v(-383.2, -16.04) * mm});
            skLineSegment(sketch, "E806", {"start": v(-372.54, -16.04) * mm, "end": v(-361.79, -16.04) * mm});
            skLineSegment(sketch, "E807", {"start": v(-351.12, -16.04) * mm, "end": v(-340.37, -16.04) * mm});
            skLineSegment(sketch, "E808", {"start": v(-329.7, -16.04) * mm, "end": v(-318.95, -16.04) * mm});
            skLineSegment(sketch, "E809", {"start": v(-308.28, -16.04) * mm, "end": v(-297.53, -16.04) * mm});
            skLineSegment(sketch, "E810", {"start": v(-244.02, -16.04) * mm, "end": v(-233.26, -16.04) * mm});
            skLineSegment(sketch, "E811", {"start": v(-222.6, -16.04) * mm, "end": v(-211.84, -16.04) * mm});
            skLineSegment(sketch, "E812", {"start": v(-158.33, -16.04) * mm, "end": v(-147.58, -16.04) * mm});
            skLineSegment(sketch, "E813", {"start": v(-51.23, -16.04) * mm, "end": v(-40.48, -16.04) * mm});
            skLineSegment(sketch, "E814", {"start": v(13.03, -16.04) * mm, "end": v(23.78, -16.04) * mm});
            skLineSegment(sketch, "E815", {"start": v(-286.86, -16.04) * mm, "end": v(-276.1, -16.04) * mm});
            skLineSegment(sketch, "E816", {"start": v(-265.44, -16.04) * mm, "end": v(-254.68, -16.04) * mm});
            skLineSegment(sketch, "E817", {"start": v(-201.17, -16.04) * mm, "end": v(-190.42, -16.04) * mm});
            skLineSegment(sketch, "E818", {"start": v(-179.75, -16.04) * mm, "end": v(-169, -16.04) * mm});
            skLineSegment(sketch, "E819", {"start": v(-136.91, -16.04) * mm, "end": v(-126.16, -16.04) * mm});
            skLineSegment(sketch, "E820", {"start": v(-115.5, -16.04) * mm, "end": v(-104.74, -16.04) * mm});
            skLineSegment(sketch, "E821", {"start": v(-94.07, -16.04) * mm, "end": v(-83.32, -16.04) * mm});
            skLineSegment(sketch, "E822", {"start": v(-72.65, -16.04) * mm, "end": v(-61.9, -16.04) * mm});
            skLineSegment(sketch, "E823", {"start": v(-29.8, -16.04) * mm, "end": v(-19.06, -16.04) * mm});
            skLineSegment(sketch, "E824", {"start": v(-8.39, -16.04) * mm, "end": v(2.36, -16.04) * mm});
            skLineSegment(sketch, "E825", {"start": v(34.45, -16.04) * mm, "end": v(45.2, -16.04) * mm});
            skLineSegment(sketch, "E826", {"start": v(55.87, -16.04) * mm, "end": v(66.63, -16.04) * mm});
            skLineSegment(sketch, "E827", {"start": v(77.3, -16.04) * mm, "end": v(88.05, -16.04) * mm});
            skLineSegment(sketch, "E828", {"start": v(98.71, -16.04) * mm, "end": v(109.47, -16.04) * mm});
            skLineSegment(sketch, "E829", {"start": v(120.14, -16.04) * mm, "end": v(130.89, -16.04) * mm});
            skLineSegment(sketch, "E830", {"start": v(141.56, -16.04) * mm, "end": v(152.3, -16.04) * mm});
            skLineSegment(sketch, "E831", {"start": v(162.98, -16.04) * mm, "end": v(173.73, -16.04) * mm});
            skLineSegment(sketch, "E832", {"start": v(184.4, -16.04) * mm, "end": v(195.15, -16.04) * mm});
            skLineSegment(sketch, "E833", {"start": v(205.82, -16.04) * mm, "end": v(216.57, -16.04) * mm});
            skLineSegment(sketch, "E834", {"start": v(227.24, -16.04) * mm, "end": v(238, -16.04) * mm});
            skLineSegment(sketch, "E835", {"start": v(248.66, -16.04) * mm, "end": v(259.41, -16.04) * mm});
            skLineSegment(sketch, "E836", {"start": v(270.08, -16.04) * mm, "end": v(280.83, -16.04) * mm});
            skLineSegment(sketch, "E837", {"start": v(291.5, -16.04) * mm, "end": v(302.25, -16.04) * mm});
            skLineSegment(sketch, "E838", {"start": v(312.92, -16.04) * mm, "end": v(323.67, -16.04) * mm});
            skLineSegment(sketch, "E839", {"start": v(334.34, -16.04) * mm, "end": v(345.1, -16.04) * mm});
            skLineSegment(sketch, "E840", {"start": v(313.63, -452.51) * mm, "end": v(-446.85, -452.51) * mm});
            skLineSegment(sketch, "E841", {"start": v(377.9, -452.51) * mm, "end": v(367.14, -452.51) * mm});
            skLineSegment(sketch, "E842", {"start": v(367.14, -452.51) * mm, "end": v(367.14, -455.51) * mm});
            skLineSegment(sketch, "E843", {"start": v(367.14, -455.51) * mm, "end": v(356.47, -455.51) * mm});
            skLineSegment(sketch, "E844", {"start": v(356.47, -455.51) * mm, "end": v(356.47, -452.51) * mm});
            skLineSegment(sketch, "E845", {"start": v(356.47, -452.51) * mm, "end": v(345.72, -452.51) * mm});
            skLineSegment(sketch, "E846", {"start": v(345.72, -452.51) * mm, "end": v(345.72, -455.51) * mm});
            skLineSegment(sketch, "E847", {"start": v(345.72, -455.51) * mm, "end": v(335.05, -455.51) * mm});
            skLineSegment(sketch, "E848", {"start": v(335.05, -455.51) * mm, "end": v(335.05, -452.51) * mm});
            skLineSegment(sketch, "E849", {"start": v(335.05, -452.51) * mm, "end": v(324.3, -452.51) * mm});
            skLineSegment(sketch, "E850", {"start": v(324.3, -452.51) * mm, "end": v(324.3, -455.51) * mm});
            skLineSegment(sketch, "E851", {"start": v(324.3, -455.51) * mm, "end": v(313.63, -455.51) * mm});
            skLineSegment(sketch, "E852", {"start": v(313.63, -455.51) * mm, "end": v(313.63, -452.51) * mm});
            skLineSegment(sketch, "E853", {"start": v(-446.85, -452.51) * mm, "end": v(-446.85, -455.51) * mm});
            skLineSegment(sketch, "E854", {"start": v(-446.85, -455.51) * mm, "end": v(-457.51, -455.51) * mm});
            skLineSegment(sketch, "E855", {"start": v(-457.51, -455.51) * mm, "end": v(-457.51, -452.51) * mm});
            skLineSegment(sketch, "E856", {"start": v(-457.51, -452.51) * mm, "end": v(-468.27, -452.51) * mm});
            skLineSegment(sketch, "E857", {"start": v(-468.27, -452.51) * mm, "end": v(-468.27, -455.51) * mm});
            skLineSegment(sketch, "E858", {"start": v(-468.27, -455.51) * mm, "end": v(-478.93, -455.51) * mm});
            skLineSegment(sketch, "E859", {"start": v(-478.93, -455.51) * mm, "end": v(-478.93, -452.51) * mm});
            skLineSegment(sketch, "E860", {"start": v(-478.93, -452.51) * mm, "end": v(-489.69, -452.51) * mm});
            skLineSegment(sketch, "E861", {"start": v(-489.69, -452.51) * mm, "end": v(-489.69, -455.51) * mm});
            skLineSegment(sketch, "E862", {"start": v(-489.69, -455.51) * mm, "end": v(-500.36, -455.51) * mm});
            skLineSegment(sketch, "E863", {"start": v(-500.36, -455.51) * mm, "end": v(-500.36, -452.51) * mm});
            skLineSegment(sketch, "E864", {"start": v(-500.36, -452.51) * mm, "end": v(-511.1, -452.51) * mm});
            skLineSegment(sketch, "E865", {"start": v(-511.1, -452.51) * mm, "end": v(-511.1, -438.62) * mm});
            skLineSegment(sketch, "E866", {"start": v(-511.1, -438.62) * mm, "end": v(-508.11, -438.62) * mm});
            skLineSegment(sketch, "E867", {"start": v(-508.11, -438.62) * mm, "end": v(-508.11, -427.95) * mm});
            skLineSegment(sketch, "E868", {"start": v(-508.11, -427.95) * mm, "end": v(-511.1, -427.95) * mm});
            skLineSegment(sketch, "E869", {"start": v(-511.1, -427.95) * mm, "end": v(-511.1, -414.06) * mm});
            skLineSegment(sketch, "E870", {"start": v(-511.1, -414.06) * mm, "end": v(-500.36, -414.06) * mm});
            skLineSegment(sketch, "E871", {"start": v(-500.36, -414.06) * mm, "end": v(-500.36, -411.06) * mm});
            skLineSegment(sketch, "E872", {"start": v(-489.69, -411.06) * mm, "end": v(-489.69, -414.06) * mm});
            skLineSegment(sketch, "E873", {"start": v(-489.69, -414.06) * mm, "end": v(-478.93, -414.06) * mm});
            skLineSegment(sketch, "E874", {"start": v(-478.93, -414.06) * mm, "end": v(-478.93, -411.06) * mm});
            skLineSegment(sketch, "E875", {"start": v(-468.27, -411.06) * mm, "end": v(-468.27, -414.06) * mm});
            skLineSegment(sketch, "E876", {"start": v(-468.27, -414.06) * mm, "end": v(-457.51, -414.06) * mm});
            skLineSegment(sketch, "E877", {"start": v(-457.51, -414.06) * mm, "end": v(-457.51, -411.06) * mm});
            skLineSegment(sketch, "E878", {"start": v(-446.85, -411.06) * mm, "end": v(-446.85, -414.06) * mm});
            skLineSegment(sketch, "E879", {"start": v(-446.85, -414.06) * mm, "end": v(-436.1, -414.06) * mm});
            skLineSegment(sketch, "E880", {"start": v(-436.1, -414.06) * mm, "end": v(-436.1, -411.06) * mm});
            skLineSegment(sketch, "E881", {"start": v(-425.43, -411.06) * mm, "end": v(-425.43, -414.06) * mm});
            skLineSegment(sketch, "E882", {"start": v(-425.43, -414.06) * mm, "end": v(-414.67, -414.06) * mm});
            skLineSegment(sketch, "E883", {"start": v(-414.67, -414.06) * mm, "end": v(-414.67, -411.06) * mm});
            skLineSegment(sketch, "E884", {"start": v(-404, -411.06) * mm, "end": v(-404, -414.06) * mm});
            skLineSegment(sketch, "E885", {"start": v(-404, -414.06) * mm, "end": v(-393.25, -414.06) * mm});
            skLineSegment(sketch, "E886", {"start": v(-393.25, -414.06) * mm, "end": v(-393.25, -411.06) * mm});
            skLineSegment(sketch, "E887", {"start": v(-382.58, -411.06) * mm, "end": v(-382.58, -414.06) * mm});
            skLineSegment(sketch, "E888", {"start": v(-382.58, -414.06) * mm, "end": v(-371.83, -414.06) * mm});
            skLineSegment(sketch, "E889", {"start": v(-371.83, -414.06) * mm, "end": v(-371.83, -411.06) * mm});
            skLineSegment(sketch, "E890", {"start": v(-361.16, -411.06) * mm, "end": v(-361.16, -414.06) * mm});
            skLineSegment(sketch, "E891", {"start": v(-361.16, -414.06) * mm, "end": v(-350.41, -414.06) * mm});
            skLineSegment(sketch, "E892", {"start": v(-350.41, -414.06) * mm, "end": v(-350.41, -411.06) * mm});
            skLineSegment(sketch, "E893", {"start": v(-339.74, -411.06) * mm, "end": v(-339.74, -414.06) * mm});
            skLineSegment(sketch, "E894", {"start": v(-339.74, -414.06) * mm, "end": v(-328.99, -414.06) * mm});
            skLineSegment(sketch, "E895", {"start": v(-328.99, -414.06) * mm, "end": v(-328.99, -411.06) * mm});
            skLineSegment(sketch, "E896", {"start": v(-318.32, -411.06) * mm, "end": v(-318.32, -414.06) * mm});
            skLineSegment(sketch, "E897", {"start": v(-318.32, -414.06) * mm, "end": v(-307.57, -414.06) * mm});
            skLineSegment(sketch, "E898", {"start": v(-307.57, -414.06) * mm, "end": v(-307.57, -411.06) * mm});
            skLineSegment(sketch, "E899", {"start": v(-296.9, -411.06) * mm, "end": v(-296.9, -414.06) * mm});
            skLineSegment(sketch, "E900", {"start": v(-296.9, -414.06) * mm, "end": v(-286.15, -414.06) * mm});
            skLineSegment(sketch, "E901", {"start": v(-286.15, -414.06) * mm, "end": v(-286.15, -411.06) * mm});
            skLineSegment(sketch, "E902", {"start": v(-275.48, -411.06) * mm, "end": v(-275.48, -414.06) * mm});
            skLineSegment(sketch, "E903", {"start": v(-275.48, -414.06) * mm, "end": v(-264.73, -414.06) * mm});
            skLineSegment(sketch, "E904", {"start": v(-264.73, -414.06) * mm, "end": v(-264.73, -411.06) * mm});
            skLineSegment(sketch, "E905", {"start": v(-254.06, -411.06) * mm, "end": v(-254.06, -414.06) * mm});
            skLineSegment(sketch, "E906", {"start": v(-254.06, -414.06) * mm, "end": v(-243.3, -414.06) * mm});
            skLineSegment(sketch, "E907", {"start": v(-243.3, -414.06) * mm, "end": v(-243.3, -411.06) * mm});
            skLineSegment(sketch, "E908", {"start": v(-232.64, -411.06) * mm, "end": v(-232.64, -414.06) * mm});
            skLineSegment(sketch, "E909", {"start": v(-232.64, -414.06) * mm, "end": v(-221.89, -414.06) * mm});
            skLineSegment(sketch, "E910", {"start": v(-221.89, -414.06) * mm, "end": v(-221.89, -411.06) * mm});
            skLineSegment(sketch, "E911", {"start": v(-211.22, -411.06) * mm, "end": v(-211.22, -414.06) * mm});
            skLineSegment(sketch, "E912", {"start": v(-211.22, -414.06) * mm, "end": v(-200.47, -414.06) * mm});
            skLineSegment(sketch, "E913", {"start": v(-200.47, -414.06) * mm, "end": v(-200.47, -411.06) * mm});
            skLineSegment(sketch, "E914", {"start": v(-189.8, -411.06) * mm, "end": v(-189.8, -414.06) * mm});
            skLineSegment(sketch, "E915", {"start": v(-189.8, -414.06) * mm, "end": v(-179.05, -414.06) * mm});
            skLineSegment(sketch, "E916", {"start": v(-179.05, -414.06) * mm, "end": v(-179.05, -411.06) * mm});
            skLineSegment(sketch, "E917", {"start": v(-168.38, -411.06) * mm, "end": v(-168.38, -414.06) * mm});
            skLineSegment(sketch, "E918", {"start": v(-168.38, -414.06) * mm, "end": v(-157.62, -414.06) * mm});
            skLineSegment(sketch, "E919", {"start": v(-157.62, -414.06) * mm, "end": v(-157.62, -411.06) * mm});
            skLineSegment(sketch, "E920", {"start": v(-146.96, -411.06) * mm, "end": v(-146.96, -414.06) * mm});
            skLineSegment(sketch, "E921", {"start": v(-146.96, -414.06) * mm, "end": v(-136.2, -414.06) * mm});
            skLineSegment(sketch, "E922", {"start": v(-136.2, -414.06) * mm, "end": v(-136.2, -411.06) * mm});
            skLineSegment(sketch, "E923", {"start": v(-125.54, -411.06) * mm, "end": v(-125.54, -414.06) * mm});
            skLineSegment(sketch, "E924", {"start": v(-125.54, -414.06) * mm, "end": v(-114.78, -414.06) * mm});
            skLineSegment(sketch, "E925", {"start": v(-114.78, -414.06) * mm, "end": v(-114.78, -411.06) * mm});
            skLineSegment(sketch, "E926", {"start": v(-104.12, -411.06) * mm, "end": v(-104.12, -414.06) * mm});
            skLineSegment(sketch, "E927", {"start": v(-104.12, -414.06) * mm, "end": v(-93.36, -414.06) * mm});
            skLineSegment(sketch, "E928", {"start": v(-93.36, -414.06) * mm, "end": v(-93.36, -411.06) * mm});
            skLineSegment(sketch, "E929", {"start": v(-82.7, -411.06) * mm, "end": v(-82.7, -414.06) * mm});
            skLineSegment(sketch, "E930", {"start": v(-82.7, -414.06) * mm, "end": v(-71.94, -414.06) * mm});
            skLineSegment(sketch, "E931", {"start": v(-71.94, -414.06) * mm, "end": v(-71.94, -411.06) * mm});
            skLineSegment(sketch, "E932", {"start": v(-61.27, -411.06) * mm, "end": v(-61.27, -414.06) * mm});
            skLineSegment(sketch, "E933", {"start": v(-61.27, -414.06) * mm, "end": v(-50.52, -414.06) * mm});
            skLineSegment(sketch, "E934", {"start": v(-50.52, -414.06) * mm, "end": v(-50.52, -411.06) * mm});
            skLineSegment(sketch, "E935", {"start": v(-39.85, -411.06) * mm, "end": v(-39.85, -414.06) * mm});
            skLineSegment(sketch, "E936", {"start": v(-39.85, -414.06) * mm, "end": v(-29.1, -414.06) * mm});
            skLineSegment(sketch, "E937", {"start": v(-29.1, -414.06) * mm, "end": v(-29.1, -411.06) * mm});
            skLineSegment(sketch, "E938", {"start": v(-18.43, -411.06) * mm, "end": v(-18.43, -414.06) * mm});
            skLineSegment(sketch, "E939", {"start": v(-18.43, -414.06) * mm, "end": v(-7.68, -414.06) * mm});
            skLineSegment(sketch, "E940", {"start": v(-7.68, -414.06) * mm, "end": v(-7.68, -411.06) * mm});
            skLineSegment(sketch, "E941", {"start": v(2.99, -411.06) * mm, "end": v(2.99, -414.06) * mm});
            skLineSegment(sketch, "E942", {"start": v(2.99, -414.06) * mm, "end": v(13.74, -414.06) * mm});
            skLineSegment(sketch, "E943", {"start": v(13.74, -414.06) * mm, "end": v(13.74, -411.06) * mm});
            skLineSegment(sketch, "E944", {"start": v(24.4, -411.06) * mm, "end": v(24.4, -414.06) * mm});
            skLineSegment(sketch, "E945", {"start": v(24.4, -414.06) * mm, "end": v(35.16, -414.06) * mm});
            skLineSegment(sketch, "E946", {"start": v(35.16, -414.06) * mm, "end": v(35.16, -411.06) * mm});
            skLineSegment(sketch, "E947", {"start": v(45.83, -411.06) * mm, "end": v(45.83, -414.06) * mm});
            skLineSegment(sketch, "E948", {"start": v(45.83, -414.06) * mm, "end": v(56.58, -414.06) * mm});
            skLineSegment(sketch, "E949", {"start": v(56.58, -414.06) * mm, "end": v(56.58, -411.06) * mm});
            skLineSegment(sketch, "E950", {"start": v(67.25, -411.06) * mm, "end": v(67.25, -414.06) * mm});
            skLineSegment(sketch, "E951", {"start": v(67.25, -414.06) * mm, "end": v(78, -414.06) * mm});
            skLineSegment(sketch, "E952", {"start": v(78, -414.06) * mm, "end": v(78, -411.06) * mm});
            skLineSegment(sketch, "E953", {"start": v(88.67, -411.06) * mm, "end": v(88.67, -414.06) * mm});
            skLineSegment(sketch, "E954", {"start": v(88.67, -414.06) * mm, "end": v(99.42, -414.06) * mm});
            skLineSegment(sketch, "E955", {"start": v(99.42, -414.06) * mm, "end": v(99.42, -411.06) * mm});
            skLineSegment(sketch, "E956", {"start": v(110.1, -411.06) * mm, "end": v(110.1, -414.06) * mm});
            skLineSegment(sketch, "E957", {"start": v(110.1, -414.06) * mm, "end": v(120.84, -414.06) * mm});
            skLineSegment(sketch, "E958", {"start": v(120.84, -414.06) * mm, "end": v(120.84, -411.06) * mm});
            skLineSegment(sketch, "E959", {"start": v(131.51, -411.06) * mm, "end": v(131.51, -414.06) * mm});
            skLineSegment(sketch, "E960", {"start": v(131.51, -414.06) * mm, "end": v(142.26, -414.06) * mm});
            skLineSegment(sketch, "E961", {"start": v(142.26, -414.06) * mm, "end": v(142.26, -411.06) * mm});
            skLineSegment(sketch, "E962", {"start": v(152.93, -411.06) * mm, "end": v(152.93, -414.06) * mm});
            skLineSegment(sketch, "E963", {"start": v(152.93, -414.06) * mm, "end": v(163.69, -414.06) * mm});
            skLineSegment(sketch, "E964", {"start": v(163.69, -414.06) * mm, "end": v(163.69, -411.06) * mm});
            skLineSegment(sketch, "E965", {"start": v(174.35, -411.06) * mm, "end": v(174.35, -414.06) * mm});
            skLineSegment(sketch, "E966", {"start": v(174.35, -414.06) * mm, "end": v(185.1, -414.06) * mm});
            skLineSegment(sketch, "E967", {"start": v(185.1, -414.06) * mm, "end": v(185.1, -411.06) * mm});
            skLineSegment(sketch, "E968", {"start": v(195.77, -411.06) * mm, "end": v(195.77, -414.06) * mm});
            skLineSegment(sketch, "E969", {"start": v(195.77, -414.06) * mm, "end": v(206.53, -414.06) * mm});
            skLineSegment(sketch, "E970", {"start": v(206.53, -414.06) * mm, "end": v(206.53, -411.06) * mm});
            skLineSegment(sketch, "E971", {"start": v(217.2, -411.06) * mm, "end": v(217.2, -414.06) * mm});
            skLineSegment(sketch, "E972", {"start": v(217.2, -414.06) * mm, "end": v(227.95, -414.06) * mm});
            skLineSegment(sketch, "E973", {"start": v(227.95, -414.06) * mm, "end": v(227.95, -411.06) * mm});
            skLineSegment(sketch, "E974", {"start": v(238.62, -411.06) * mm, "end": v(238.62, -414.06) * mm});
            skLineSegment(sketch, "E975", {"start": v(238.62, -414.06) * mm, "end": v(249.37, -414.06) * mm});
            skLineSegment(sketch, "E976", {"start": v(249.37, -414.06) * mm, "end": v(249.37, -411.06) * mm});
            skLineSegment(sketch, "E977", {"start": v(260.04, -411.06) * mm, "end": v(260.04, -414.06) * mm});
            skLineSegment(sketch, "E978", {"start": v(260.04, -414.06) * mm, "end": v(270.79, -414.06) * mm});
            skLineSegment(sketch, "E979", {"start": v(270.79, -414.06) * mm, "end": v(270.79, -411.06) * mm});
            skLineSegment(sketch, "E980", {"start": v(281.46, -411.06) * mm, "end": v(281.46, -414.06) * mm});
            skLineSegment(sketch, "E981", {"start": v(281.46, -414.06) * mm, "end": v(292.2, -414.06) * mm});
            skLineSegment(sketch, "E982", {"start": v(292.2, -414.06) * mm, "end": v(292.2, -411.06) * mm});
            skLineSegment(sketch, "E983", {"start": v(302.88, -411.06) * mm, "end": v(302.88, -414.06) * mm});
            skLineSegment(sketch, "E984", {"start": v(302.88, -414.06) * mm, "end": v(313.63, -414.06) * mm});
            skLineSegment(sketch, "E985", {"start": v(313.63, -414.06) * mm, "end": v(313.63, -411.06) * mm});
            skLineSegment(sketch, "E986", {"start": v(324.3, -411.06) * mm, "end": v(324.3, -414.06) * mm});
            skLineSegment(sketch, "E987", {"start": v(324.3, -414.06) * mm, "end": v(335.05, -414.06) * mm});
            skLineSegment(sketch, "E988", {"start": v(335.05, -414.06) * mm, "end": v(335.05, -411.06) * mm});
            skLineSegment(sketch, "E989", {"start": v(345.72, -411.06) * mm, "end": v(345.72, -414.06) * mm});
            skLineSegment(sketch, "E990", {"start": v(345.72, -414.06) * mm, "end": v(356.47, -414.06) * mm});
            skLineSegment(sketch, "E991", {"start": v(356.47, -414.06) * mm, "end": v(356.47, -411.06) * mm});
            skLineSegment(sketch, "E992", {"start": v(367.14, -411.06) * mm, "end": v(367.14, -414.06) * mm});
            skLineSegment(sketch, "E993", {"start": v(367.14, -414.06) * mm, "end": v(377.9, -414.06) * mm});
            skLineSegment(sketch, "E994", {"start": v(377.9, -414.06) * mm, "end": v(377.9, -427.95) * mm});
            skLineSegment(sketch, "E995", {"start": v(377.9, -427.95) * mm, "end": v(374.9, -427.95) * mm});
            skLineSegment(sketch, "E996", {"start": v(374.9, -427.95) * mm, "end": v(374.9, -438.62) * mm});
            skLineSegment(sketch, "E997", {"start": v(374.9, -438.62) * mm, "end": v(377.9, -438.62) * mm});
            skLineSegment(sketch, "E998", {"start": v(377.9, -438.62) * mm, "end": v(377.9, -452.51) * mm});
            skCircle(sketch, "E999", {"center": v(-287.36, -438.62) * mm, "radius": 2.18 * mm});
            skCircle(sketch, "E1000", {"center": v(154.14, -438.62) * mm, "radius": 2.18 * mm});
            skLineSegment(sketch, "E1001", {"start": v(356.47, -411.06) * mm, "end": v(345.72, -411.06) * mm});
            skLineSegment(sketch, "E1002", {"start": v(335.05, -411.06) * mm, "end": v(324.3, -411.06) * mm});
            skLineSegment(sketch, "E1003", {"start": v(313.63, -411.06) * mm, "end": v(302.88, -411.06) * mm});
            skLineSegment(sketch, "E1004", {"start": v(292.2, -411.06) * mm, "end": v(281.46, -411.06) * mm});
            skLineSegment(sketch, "E1005", {"start": v(270.79, -411.06) * mm, "end": v(260.04, -411.06) * mm});
            skLineSegment(sketch, "E1006", {"start": v(249.37, -411.06) * mm, "end": v(238.62, -411.06) * mm});
            skLineSegment(sketch, "E1007", {"start": v(227.95, -411.06) * mm, "end": v(217.2, -411.06) * mm});
            skLineSegment(sketch, "E1008", {"start": v(206.53, -411.06) * mm, "end": v(195.77, -411.06) * mm});
            skLineSegment(sketch, "E1009", {"start": v(185.1, -411.06) * mm, "end": v(174.35, -411.06) * mm});
            skLineSegment(sketch, "E1010", {"start": v(163.69, -411.06) * mm, "end": v(152.93, -411.06) * mm});
            skLineSegment(sketch, "E1011", {"start": v(99.42, -411.06) * mm, "end": v(88.67, -411.06) * mm});
            skLineSegment(sketch, "E1012", {"start": v(78, -411.06) * mm, "end": v(67.25, -411.06) * mm});
            skLineSegment(sketch, "E1013", {"start": v(13.74, -411.06) * mm, "end": v(2.99, -411.06) * mm});
            skLineSegment(sketch, "E1014", {"start": v(-93.36, -411.06) * mm, "end": v(-104.12, -411.06) * mm});
            skLineSegment(sketch, "E1015", {"start": v(-157.62, -411.06) * mm, "end": v(-168.38, -411.06) * mm});
            skLineSegment(sketch, "E1016", {"start": v(142.26, -411.06) * mm, "end": v(131.51, -411.06) * mm});
            skLineSegment(sketch, "E1017", {"start": v(120.84, -411.06) * mm, "end": v(110.1, -411.06) * mm});
            skLineSegment(sketch, "E1018", {"start": v(56.58, -411.06) * mm, "end": v(45.83, -411.06) * mm});
            skLineSegment(sketch, "E1019", {"start": v(35.16, -411.06) * mm, "end": v(24.4, -411.06) * mm});
            skLineSegment(sketch, "E1020", {"start": v(-7.68, -411.06) * mm, "end": v(-18.43, -411.06) * mm});
            skLineSegment(sketch, "E1021", {"start": v(-29.1, -411.06) * mm, "end": v(-39.85, -411.06) * mm});
            skLineSegment(sketch, "E1022", {"start": v(-50.52, -411.06) * mm, "end": v(-61.27, -411.06) * mm});
            skLineSegment(sketch, "E1023", {"start": v(-71.94, -411.06) * mm, "end": v(-82.7, -411.06) * mm});
            skLineSegment(sketch, "E1024", {"start": v(-114.78, -411.06) * mm, "end": v(-125.54, -411.06) * mm});
            skLineSegment(sketch, "E1025", {"start": v(-136.2, -411.06) * mm, "end": v(-146.96, -411.06) * mm});
            skLineSegment(sketch, "E1026", {"start": v(-179.05, -411.06) * mm, "end": v(-189.8, -411.06) * mm});
            skLineSegment(sketch, "E1027", {"start": v(-200.47, -411.06) * mm, "end": v(-211.22, -411.06) * mm});
            skLineSegment(sketch, "E1028", {"start": v(-221.89, -411.06) * mm, "end": v(-232.64, -411.06) * mm});
            skLineSegment(sketch, "E1029", {"start": v(-243.3, -411.06) * mm, "end": v(-254.06, -411.06) * mm});
            skLineSegment(sketch, "E1030", {"start": v(-264.73, -411.06) * mm, "end": v(-275.48, -411.06) * mm});
            skLineSegment(sketch, "E1031", {"start": v(-286.15, -411.06) * mm, "end": v(-296.9, -411.06) * mm});
            skLineSegment(sketch, "E1032", {"start": v(-307.57, -411.06) * mm, "end": v(-318.32, -411.06) * mm});
            skLineSegment(sketch, "E1033", {"start": v(-328.99, -411.06) * mm, "end": v(-339.74, -411.06) * mm});
            skLineSegment(sketch, "E1034", {"start": v(-350.41, -411.06) * mm, "end": v(-361.16, -411.06) * mm});
            skLineSegment(sketch, "E1035", {"start": v(-371.83, -411.06) * mm, "end": v(-382.58, -411.06) * mm});
            skLineSegment(sketch, "E1036", {"start": v(-393.25, -411.06) * mm, "end": v(-404, -411.06) * mm});
            skLineSegment(sketch, "E1037", {"start": v(-414.67, -411.06) * mm, "end": v(-425.43, -411.06) * mm});
            skLineSegment(sketch, "E1038", {"start": v(-436.1, -411.06) * mm, "end": v(-446.85, -411.06) * mm});
            skLineSegment(sketch, "E1039", {"start": v(-457.51, -411.06) * mm, "end": v(-468.27, -411.06) * mm});
            skLineSegment(sketch, "E1040", {"start": v(-478.93, -411.06) * mm, "end": v(-489.69, -411.06) * mm});
            skLineSegment(sketch, "E1041", {"start": v(-490.73, 441.98) * mm, "end": v(-490.73, 450.85) * mm});
            skLineSegment(sketch, "E1042", {"start": v(-490.73, 160.9) * mm, "end": v(-490.73, 152.04) * mm});
            skLineSegment(sketch, "E1043", {"start": v(-500.44, 152.04) * mm, "end": v(-500.44, 450.85) * mm});
            skLineSegment(sketch, "E1044", {"start": v(-490.73, 152.04) * mm, "end": v(-500.44, 152.04) * mm});
            skLineSegment(sketch, "E1045", {"start": v(-490.73, 450.85) * mm, "end": v(-500.44, 450.85) * mm});
            skLineSegment(sketch, "E1046", {"start": v(471.33, 217.48) * mm, "end": v(471.33, 387.08) * mm});
            skLineSegment(sketch, "E1047", {"start": v(471.33, 152.87) * mm, "end": v(485.22, 152.87) * mm});
            skLineSegment(sketch, "E1048", {"start": v(485.22, 152.87) * mm, "end": v(485.22, 149.88) * mm});
            skLineSegment(sketch, "E1049", {"start": v(485.22, 149.88) * mm, "end": v(495.9, 149.88) * mm});
            skLineSegment(sketch, "E1050", {"start": v(495.9, 149.88) * mm, "end": v(495.9, 152.87) * mm});
            skLineSegment(sketch, "E1051", {"start": v(495.9, 152.87) * mm, "end": v(509.78, 152.87) * mm});
            skLineSegment(sketch, "E1052", {"start": v(509.78, 152.87) * mm, "end": v(509.78, 161.74) * mm});
            skLineSegment(sketch, "E1053", {"start": v(509.78, 161.74) * mm, "end": v(512.78, 161.74) * mm});
            skLineSegment(sketch, "E1054", {"start": v(512.78, 172.41) * mm, "end": v(509.78, 172.41) * mm});
            skLineSegment(sketch, "E1055", {"start": v(509.78, 172.41) * mm, "end": v(509.78, 184.28) * mm});
            skLineSegment(sketch, "E1056", {"start": v(509.78, 184.28) * mm, "end": v(512.78, 184.28) * mm});
            skLineSegment(sketch, "E1057", {"start": v(512.78, 194.94) * mm, "end": v(509.78, 194.94) * mm});
            skLineSegment(sketch, "E1058", {"start": v(509.78, 194.94) * mm, "end": v(509.78, 206.8) * mm});
            skLineSegment(sketch, "E1059", {"start": v(509.78, 206.8) * mm, "end": v(512.78, 206.8) * mm});
            skLineSegment(sketch, "E1060", {"start": v(512.78, 217.48) * mm, "end": v(509.78, 217.48) * mm});
            skLineSegment(sketch, "E1061", {"start": v(509.78, 217.48) * mm, "end": v(509.78, 229.34) * mm});
            skLineSegment(sketch, "E1062", {"start": v(509.78, 229.34) * mm, "end": v(512.78, 229.34) * mm});
            skLineSegment(sketch, "E1063", {"start": v(512.78, 240.01) * mm, "end": v(509.78, 240.01) * mm});
            skLineSegment(sketch, "E1064", {"start": v(509.78, 240.01) * mm, "end": v(509.78, 251.88) * mm});
            skLineSegment(sketch, "E1065", {"start": v(509.78, 251.88) * mm, "end": v(512.78, 251.88) * mm});
            skLineSegment(sketch, "E1066", {"start": v(512.78, 262.54) * mm, "end": v(509.78, 262.54) * mm});
            skLineSegment(sketch, "E1067", {"start": v(509.78, 262.54) * mm, "end": v(509.78, 274.41) * mm});
            skLineSegment(sketch, "E1068", {"start": v(509.78, 274.41) * mm, "end": v(512.78, 274.41) * mm});
            skLineSegment(sketch, "E1069", {"start": v(512.78, 285.08) * mm, "end": v(509.78, 285.08) * mm});
            skLineSegment(sketch, "E1070", {"start": v(509.78, 285.08) * mm, "end": v(509.78, 296.94) * mm});
            skLineSegment(sketch, "E1071", {"start": v(509.78, 296.94) * mm, "end": v(512.78, 296.94) * mm});
            skLineSegment(sketch, "E1072", {"start": v(512.78, 307.61) * mm, "end": v(509.78, 307.61) * mm});
            skLineSegment(sketch, "E1073", {"start": v(509.78, 307.61) * mm, "end": v(509.78, 319.48) * mm});
            skLineSegment(sketch, "E1074", {"start": v(509.78, 319.48) * mm, "end": v(512.78, 319.48) * mm});
            skLineSegment(sketch, "E1075", {"start": v(512.78, 330.14) * mm, "end": v(509.78, 330.14) * mm});
            skLineSegment(sketch, "E1076", {"start": v(509.78, 330.14) * mm, "end": v(509.78, 342.01) * mm});
            skLineSegment(sketch, "E1077", {"start": v(509.78, 342.01) * mm, "end": v(512.78, 342.01) * mm});
            skLineSegment(sketch, "E1078", {"start": v(512.78, 352.68) * mm, "end": v(509.78, 352.68) * mm});
            skLineSegment(sketch, "E1079", {"start": v(509.78, 352.68) * mm, "end": v(509.78, 364.54) * mm});
            skLineSegment(sketch, "E1080", {"start": v(509.78, 364.54) * mm, "end": v(512.78, 364.54) * mm});
            skLineSegment(sketch, "E1081", {"start": v(512.78, 375.21) * mm, "end": v(509.78, 375.21) * mm});
            skLineSegment(sketch, "E1082", {"start": v(509.78, 375.21) * mm, "end": v(509.78, 387.08) * mm});
            skLineSegment(sketch, "E1083", {"start": v(509.78, 387.08) * mm, "end": v(512.78, 387.08) * mm});
            skLineSegment(sketch, "E1084", {"start": v(512.78, 397.75) * mm, "end": v(509.78, 397.75) * mm});
            skLineSegment(sketch, "E1085", {"start": v(509.78, 397.75) * mm, "end": v(509.78, 409.61) * mm});
            skLineSegment(sketch, "E1086", {"start": v(509.78, 409.61) * mm, "end": v(512.78, 409.61) * mm});
            skLineSegment(sketch, "E1087", {"start": v(512.78, 420.28) * mm, "end": v(509.78, 420.28) * mm});
            skLineSegment(sketch, "E1088", {"start": v(509.78, 420.28) * mm, "end": v(509.78, 432.14) * mm});
            skLineSegment(sketch, "E1089", {"start": v(509.78, 432.14) * mm, "end": v(512.78, 432.14) * mm});
            skLineSegment(sketch, "E1090", {"start": v(512.78, 442.81) * mm, "end": v(509.78, 442.81) * mm});
            skLineSegment(sketch, "E1091", {"start": v(509.78, 442.81) * mm, "end": v(509.78, 451.68) * mm});
            skLineSegment(sketch, "E1092", {"start": v(509.78, 451.68) * mm, "end": v(495.9, 451.68) * mm});
            skLineSegment(sketch, "E1093", {"start": v(495.9, 451.68) * mm, "end": v(495.9, 454.68) * mm});
            skLineSegment(sketch, "E1094", {"start": v(495.9, 454.68) * mm, "end": v(485.22, 454.68) * mm});
            skLineSegment(sketch, "E1095", {"start": v(485.22, 454.68) * mm, "end": v(485.22, 451.68) * mm});
            skLineSegment(sketch, "E1096", {"start": v(485.22, 451.68) * mm, "end": v(471.33, 451.68) * mm});
            skLineSegment(sketch, "E1097", {"start": v(471.33, 451.68) * mm, "end": v(471.33, 442.81) * mm});
            skLineSegment(sketch, "E1098", {"start": v(471.33, 442.81) * mm, "end": v(468.33, 442.81) * mm});
            skLineSegment(sketch, "E1099", {"start": v(468.33, 442.81) * mm, "end": v(468.33, 432.14) * mm});
            skLineSegment(sketch, "E1100", {"start": v(468.33, 432.14) * mm, "end": v(471.33, 432.14) * mm});
            skLineSegment(sketch, "E1101", {"start": v(471.33, 432.14) * mm, "end": v(471.33, 420.28) * mm});
            skLineSegment(sketch, "E1102", {"start": v(471.33, 420.28) * mm, "end": v(468.33, 420.28) * mm});
            skLineSegment(sketch, "E1103", {"start": v(468.33, 420.28) * mm, "end": v(468.33, 409.61) * mm});
            skLineSegment(sketch, "E1104", {"start": v(468.33, 409.61) * mm, "end": v(471.33, 409.61) * mm});
            skLineSegment(sketch, "E1105", {"start": v(471.33, 409.61) * mm, "end": v(471.33, 397.75) * mm});
            skLineSegment(sketch, "E1106", {"start": v(471.33, 397.75) * mm, "end": v(468.33, 397.75) * mm});
            skLineSegment(sketch, "E1107", {"start": v(468.33, 397.75) * mm, "end": v(468.33, 387.08) * mm});
            skLineSegment(sketch, "E1108", {"start": v(468.33, 387.08) * mm, "end": v(471.33, 387.08) * mm});
            skLineSegment(sketch, "E1109", {"start": v(471.33, 217.48) * mm, "end": v(468.33, 217.48) * mm});
            skLineSegment(sketch, "E1110", {"start": v(468.33, 217.48) * mm, "end": v(468.33, 206.8) * mm});
            skLineSegment(sketch, "E1111", {"start": v(468.33, 206.8) * mm, "end": v(471.33, 206.8) * mm});
            skLineSegment(sketch, "E1112", {"start": v(471.33, 206.8) * mm, "end": v(471.33, 194.94) * mm});
            skLineSegment(sketch, "E1113", {"start": v(471.33, 194.94) * mm, "end": v(468.33, 194.94) * mm});
            skLineSegment(sketch, "E1114", {"start": v(468.33, 194.94) * mm, "end": v(468.33, 184.28) * mm});
            skLineSegment(sketch, "E1115", {"start": v(468.33, 184.28) * mm, "end": v(471.33, 184.28) * mm});
            skLineSegment(sketch, "E1116", {"start": v(471.33, 184.28) * mm, "end": v(471.33, 172.41) * mm});
            skLineSegment(sketch, "E1117", {"start": v(471.33, 172.41) * mm, "end": v(468.33, 172.41) * mm});
            skLineSegment(sketch, "E1118", {"start": v(468.33, 172.41) * mm, "end": v(468.33, 161.74) * mm});
            skLineSegment(sketch, "E1119", {"start": v(468.33, 161.74) * mm, "end": v(471.33, 161.74) * mm});
            skLineSegment(sketch, "E1120", {"start": v(471.33, 161.74) * mm, "end": v(471.33, 152.87) * mm});
            skCircle(sketch, "E1121", {"center": v(478.28, 302.28) * mm, "radius": 2.18 * mm});
            skLineSegment(sketch, "E1122", {"start": v(495.64, 413.51) * mm, "end": v(485.15, 413.51) * mm});
            skLineSegment(sketch, "E1123", {"start": v(485.15, 413.51) * mm, "end": v(485.15, 438.91) * mm});
            skLineSegment(sketch, "E1124", {"start": v(485.15, 438.91) * mm, "end": v(495.64, 438.91) * mm});
            skLineSegment(sketch, "E1125", {"start": v(495.64, 438.91) * mm, "end": v(495.64, 413.51) * mm});
            skCircle(sketch, "E1126", {"center": v(490.56, 378.48) * mm, "radius": 2.08 * mm});
            skCircle(sketch, "E1127", {"center": v(490.56, 226.08) * mm, "radius": 2.08 * mm});
            skLineSegment(sketch, "E1128", {"start": v(512.78, 172.41) * mm, "end": v(512.78, 184.28) * mm});
            skLineSegment(sketch, "E1129", {"start": v(512.78, 194.94) * mm, "end": v(512.78, 206.8) * mm});
            skLineSegment(sketch, "E1130", {"start": v(512.78, 217.48) * mm, "end": v(512.78, 229.34) * mm});
            skLineSegment(sketch, "E1131", {"start": v(512.78, 240.01) * mm, "end": v(512.78, 251.88) * mm});
            skLineSegment(sketch, "E1132", {"start": v(512.78, 262.54) * mm, "end": v(512.78, 274.41) * mm});
            skLineSegment(sketch, "E1133", {"start": v(512.78, 285.08) * mm, "end": v(512.78, 296.94) * mm});
            skLineSegment(sketch, "E1134", {"start": v(512.78, 307.61) * mm, "end": v(512.78, 319.48) * mm});
            skLineSegment(sketch, "E1135", {"start": v(512.78, 352.68) * mm, "end": v(512.78, 364.54) * mm});
            skLineSegment(sketch, "E1136", {"start": v(512.78, 375.21) * mm, "end": v(512.78, 387.08) * mm});
            skLineSegment(sketch, "E1137", {"start": v(512.78, 397.75) * mm, "end": v(512.78, 409.61) * mm});
            skLineSegment(sketch, "E1138", {"start": v(512.78, 420.28) * mm, "end": v(512.78, 432.14) * mm});
            skLineSegment(sketch, "E1139", {"start": v(512.78, 330.14) * mm, "end": v(512.78, 342.01) * mm});
            skLineSegment(sketch, "E1140", {"start": v(512.78, 442.81) * mm, "end": v(512.78, 451.68) * mm});
            skLineSegment(sketch, "E1141", {"start": v(512.78, 161.74) * mm, "end": v(512.78, 152.87) * mm});
            skLineSegment(sketch, "E1142", {"start": v(522.48, 152.87) * mm, "end": v(522.48, 451.68) * mm});
            skLineSegment(sketch, "E1143", {"start": v(512.78, 152.87) * mm, "end": v(522.48, 152.87) * mm});
            skLineSegment(sketch, "E1144", {"start": v(512.78, 451.68) * mm, "end": v(522.48, 451.68) * mm});
            skCircle(sketch, "E1145", {"center": v(-460.69, -126.98) * mm, "radius": 4.57 * mm});
            skCircle(sketch, "E1146", {"center": v(-355.68, -231.99) * mm, "radius": 4.57 * mm});
            skCircle(sketch, "E1147", {"center": v(-460.69, -231.99) * mm, "radius": 4.57 * mm});
            skCircle(sketch, "E1148", {"center": v(-355.68, -126.98) * mm, "radius": 4.57 * mm});
            skLineSegment(sketch, "E1149", {"start": v(-371.35, -156.2) * mm, "end": v(-377.95, -167.62) * mm});
            skLineSegment(sketch, "E1150", {"start": v(-377.95, -167.62) * mm, "end": v(-364.76, -167.62) * mm});
            skLineSegment(sketch, "E1151", {"start": v(-364.76, -167.62) * mm, "end": v(-371.35, -156.2) * mm});
            skLineSegment(sketch, "E1152", {"start": v(-378.97, -161.27) * mm, "end": v(-372.38, -149.84) * mm});
            skLineSegment(sketch, "E1153", {"start": v(-372.38, -149.84) * mm, "end": v(-385.57, -149.84) * mm});
            skLineSegment(sketch, "E1154", {"start": v(-385.57, -149.84) * mm, "end": v(-378.97, -161.27) * mm});
            skLineSegment(sketch, "E1155", {"start": v(-363.73, -161.27) * mm, "end": v(-357.14, -149.84) * mm});
            skLineSegment(sketch, "E1156", {"start": v(-357.14, -149.84) * mm, "end": v(-370.33, -149.84) * mm});
            skLineSegment(sketch, "E1157", {"start": v(-370.33, -149.84) * mm, "end": v(-363.73, -161.27) * mm});
            skLineSegment(sketch, "E1158", {"start": v(-396.75, -161.27) * mm, "end": v(-390.16, -149.84) * mm});
            skLineSegment(sketch, "E1159", {"start": v(-390.16, -149.84) * mm, "end": v(-403.35, -149.84) * mm});
            skLineSegment(sketch, "E1160", {"start": v(-403.35, -149.84) * mm, "end": v(-396.75, -161.27) * mm});
            skLineSegment(sketch, "E1161", {"start": v(-389.13, -156.2) * mm, "end": v(-395.73, -167.62) * mm});
            skLineSegment(sketch, "E1162", {"start": v(-395.73, -167.62) * mm, "end": v(-382.54, -167.62) * mm});
            skLineSegment(sketch, "E1163", {"start": v(-382.54, -167.62) * mm, "end": v(-389.13, -156.2) * mm});
            skLineSegment(sketch, "E1164", {"start": v(-404.37, -156.2) * mm, "end": v(-410.97, -167.62) * mm});
            skLineSegment(sketch, "E1165", {"start": v(-410.97, -167.62) * mm, "end": v(-397.78, -167.62) * mm});
            skLineSegment(sketch, "E1166", {"start": v(-397.78, -167.62) * mm, "end": v(-404.37, -156.2) * mm});
            skLineSegment(sketch, "E1167", {"start": v(-419.86, -156.2) * mm, "end": v(-426.46, -167.62) * mm});
            skLineSegment(sketch, "E1168", {"start": v(-426.46, -167.62) * mm, "end": v(-413.26, -167.62) * mm});
            skLineSegment(sketch, "E1169", {"start": v(-413.26, -167.62) * mm, "end": v(-419.86, -156.2) * mm});
            skLineSegment(sketch, "E1170", {"start": v(-427.48, -161.27) * mm, "end": v(-420.88, -149.84) * mm});
            skLineSegment(sketch, "E1171", {"start": v(-420.88, -149.84) * mm, "end": v(-434.08, -149.84) * mm});
            skLineSegment(sketch, "E1172", {"start": v(-434.08, -149.84) * mm, "end": v(-427.48, -161.27) * mm});
            skLineSegment(sketch, "E1173", {"start": v(-412.24, -161.27) * mm, "end": v(-405.64, -149.84) * mm});
            skLineSegment(sketch, "E1174", {"start": v(-405.64, -149.84) * mm, "end": v(-418.84, -149.84) * mm});
            skLineSegment(sketch, "E1175", {"start": v(-418.84, -149.84) * mm, "end": v(-412.24, -161.27) * mm});
            skLineSegment(sketch, "E1176", {"start": v(-445.26, -161.27) * mm, "end": v(-438.66, -149.84) * mm});
            skLineSegment(sketch, "E1177", {"start": v(-438.66, -149.84) * mm, "end": v(-451.86, -149.84) * mm});
            skLineSegment(sketch, "E1178", {"start": v(-451.86, -149.84) * mm, "end": v(-445.26, -161.27) * mm});
            skLineSegment(sketch, "E1179", {"start": v(-437.64, -156.2) * mm, "end": v(-444.24, -167.62) * mm});
            skLineSegment(sketch, "E1180", {"start": v(-444.24, -167.62) * mm, "end": v(-431.04, -167.62) * mm});
            skLineSegment(sketch, "E1181", {"start": v(-431.04, -167.62) * mm, "end": v(-437.64, -156.2) * mm});
            skLineSegment(sketch, "E1182", {"start": v(-452.88, -156.2) * mm, "end": v(-459.48, -167.62) * mm});
            skLineSegment(sketch, "E1183", {"start": v(-459.48, -167.62) * mm, "end": v(-446.28, -167.62) * mm});
            skLineSegment(sketch, "E1184", {"start": v(-446.28, -167.62) * mm, "end": v(-452.88, -156.2) * mm});
            skLineSegment(sketch, "E1185", {"start": v(-371.35, -135.87) * mm, "end": v(-377.95, -147.3) * mm});
            skLineSegment(sketch, "E1186", {"start": v(-377.95, -147.3) * mm, "end": v(-364.76, -147.3) * mm});
            skLineSegment(sketch, "E1187", {"start": v(-364.76, -147.3) * mm, "end": v(-371.35, -135.87) * mm});
            skLineSegment(sketch, "E1188", {"start": v(-378.97, -140.95) * mm, "end": v(-372.38, -129.52) * mm});
            skLineSegment(sketch, "E1189", {"start": v(-372.38, -129.52) * mm, "end": v(-385.57, -129.52) * mm});
            skLineSegment(sketch, "E1190", {"start": v(-385.57, -129.52) * mm, "end": v(-378.97, -140.95) * mm});
            skLineSegment(sketch, "E1191", {"start": v(-370.33, -129.52) * mm, "end": v(-363.73, -140.95) * mm});
            skLineSegment(sketch, "E1192", {"start": v(-396.75, -140.95) * mm, "end": v(-390.16, -129.52) * mm});
            skLineSegment(sketch, "E1193", {"start": v(-390.16, -129.52) * mm, "end": v(-403.35, -129.52) * mm});
            skLineSegment(sketch, "E1194", {"start": v(-403.35, -129.52) * mm, "end": v(-396.75, -140.95) * mm});
            skLineSegment(sketch, "E1195", {"start": v(-389.13, -135.87) * mm, "end": v(-395.73, -147.3) * mm});
            skLineSegment(sketch, "E1196", {"start": v(-395.73, -147.3) * mm, "end": v(-382.54, -147.3) * mm});
            skLineSegment(sketch, "E1197", {"start": v(-382.54, -147.3) * mm, "end": v(-389.13, -135.87) * mm});
            skLineSegment(sketch, "E1198", {"start": v(-404.37, -135.87) * mm, "end": v(-410.97, -147.3) * mm});
            skLineSegment(sketch, "E1199", {"start": v(-410.97, -147.3) * mm, "end": v(-397.78, -147.3) * mm});
            skLineSegment(sketch, "E1200", {"start": v(-397.78, -147.3) * mm, "end": v(-404.37, -135.87) * mm});
            skLineSegment(sketch, "E1201", {"start": v(-419.86, -135.87) * mm, "end": v(-426.46, -147.3) * mm});
            skLineSegment(sketch, "E1202", {"start": v(-426.46, -147.3) * mm, "end": v(-413.26, -147.3) * mm});
            skLineSegment(sketch, "E1203", {"start": v(-413.26, -147.3) * mm, "end": v(-419.86, -135.87) * mm});
            skLineSegment(sketch, "E1204", {"start": v(-427.48, -140.95) * mm, "end": v(-420.88, -129.52) * mm});
            skLineSegment(sketch, "E1205", {"start": v(-420.88, -129.52) * mm, "end": v(-434.08, -129.52) * mm});
            skLineSegment(sketch, "E1206", {"start": v(-434.08, -129.52) * mm, "end": v(-427.48, -140.95) * mm});
            skLineSegment(sketch, "E1207", {"start": v(-412.24, -140.95) * mm, "end": v(-405.64, -129.52) * mm});
            skLineSegment(sketch, "E1208", {"start": v(-405.64, -129.52) * mm, "end": v(-418.84, -129.52) * mm});
            skLineSegment(sketch, "E1209", {"start": v(-418.84, -129.52) * mm, "end": v(-412.24, -140.95) * mm});
            skLineSegment(sketch, "E1210", {"start": v(-445.26, -140.95) * mm, "end": v(-438.66, -129.52) * mm});
            skLineSegment(sketch, "E1211", {"start": v(-438.66, -129.52) * mm, "end": v(-451.86, -129.52) * mm});
            skLineSegment(sketch, "E1212", {"start": v(-451.86, -129.52) * mm, "end": v(-445.26, -140.95) * mm});
            skLineSegment(sketch, "E1213", {"start": v(-437.64, -135.87) * mm, "end": v(-444.24, -147.3) * mm});
            skLineSegment(sketch, "E1214", {"start": v(-444.24, -147.3) * mm, "end": v(-431.04, -147.3) * mm});
            skLineSegment(sketch, "E1215", {"start": v(-431.04, -147.3) * mm, "end": v(-437.64, -135.87) * mm});
            skLineSegment(sketch, "E1216", {"start": v(-452.88, -135.87) * mm, "end": v(-459.48, -147.3) * mm});
            skLineSegment(sketch, "E1217", {"start": v(-459.48, -147.3) * mm, "end": v(-446.28, -147.3) * mm});
            skLineSegment(sketch, "E1218", {"start": v(-446.28, -147.3) * mm, "end": v(-452.88, -135.87) * mm});
            skLineSegment(sketch, "E1219", {"start": v(-371.35, -196.83) * mm, "end": v(-377.95, -208.26) * mm});
            skLineSegment(sketch, "E1220", {"start": v(-377.95, -208.26) * mm, "end": v(-364.76, -208.26) * mm});
            skLineSegment(sketch, "E1221", {"start": v(-364.76, -208.26) * mm, "end": v(-371.35, -196.83) * mm});
            skLineSegment(sketch, "E1222", {"start": v(-378.97, -201.91) * mm, "end": v(-372.38, -190.48) * mm});
            skLineSegment(sketch, "E1223", {"start": v(-372.38, -190.48) * mm, "end": v(-385.57, -190.48) * mm});
            skLineSegment(sketch, "E1224", {"start": v(-385.57, -190.48) * mm, "end": v(-378.97, -201.91) * mm});
            skLineSegment(sketch, "E1225", {"start": v(-363.73, -201.91) * mm, "end": v(-357.14, -190.48) * mm});
            skLineSegment(sketch, "E1226", {"start": v(-357.14, -190.48) * mm, "end": v(-370.33, -190.48) * mm});
            skLineSegment(sketch, "E1227", {"start": v(-370.33, -190.48) * mm, "end": v(-363.73, -201.91) * mm});
            skLineSegment(sketch, "E1228", {"start": v(-396.75, -201.91) * mm, "end": v(-390.16, -190.48) * mm});
            skLineSegment(sketch, "E1229", {"start": v(-390.16, -190.48) * mm, "end": v(-403.35, -190.48) * mm});
            skLineSegment(sketch, "E1230", {"start": v(-403.35, -190.48) * mm, "end": v(-396.75, -201.91) * mm});
            skLineSegment(sketch, "E1231", {"start": v(-389.13, -196.83) * mm, "end": v(-395.73, -208.26) * mm});
            skLineSegment(sketch, "E1232", {"start": v(-395.73, -208.26) * mm, "end": v(-382.54, -208.26) * mm});
            skLineSegment(sketch, "E1233", {"start": v(-382.54, -208.26) * mm, "end": v(-389.13, -196.83) * mm});
            skLineSegment(sketch, "E1234", {"start": v(-404.37, -196.83) * mm, "end": v(-410.97, -208.26) * mm});
            skLineSegment(sketch, "E1235", {"start": v(-410.97, -208.26) * mm, "end": v(-397.78, -208.26) * mm});
            skLineSegment(sketch, "E1236", {"start": v(-397.78, -208.26) * mm, "end": v(-404.37, -196.83) * mm});
            skLineSegment(sketch, "E1237", {"start": v(-419.86, -196.83) * mm, "end": v(-426.46, -208.26) * mm});
            skLineSegment(sketch, "E1238", {"start": v(-426.46, -208.26) * mm, "end": v(-413.26, -208.26) * mm});
            skLineSegment(sketch, "E1239", {"start": v(-413.26, -208.26) * mm, "end": v(-419.86, -196.83) * mm});
            skLineSegment(sketch, "E1240", {"start": v(-427.48, -201.91) * mm, "end": v(-420.88, -190.48) * mm});
            skLineSegment(sketch, "E1241", {"start": v(-420.88, -190.48) * mm, "end": v(-434.08, -190.48) * mm});
            skLineSegment(sketch, "E1242", {"start": v(-434.08, -190.48) * mm, "end": v(-427.48, -201.91) * mm});
            skLineSegment(sketch, "E1243", {"start": v(-412.24, -201.91) * mm, "end": v(-405.64, -190.48) * mm});
            skLineSegment(sketch, "E1244", {"start": v(-405.64, -190.48) * mm, "end": v(-418.84, -190.48) * mm});
            skLineSegment(sketch, "E1245", {"start": v(-418.84, -190.48) * mm, "end": v(-412.24, -201.91) * mm});
            skLineSegment(sketch, "E1246", {"start": v(-445.26, -201.91) * mm, "end": v(-438.66, -190.48) * mm});
            skLineSegment(sketch, "E1247", {"start": v(-438.66, -190.48) * mm, "end": v(-451.86, -190.48) * mm});
            skLineSegment(sketch, "E1248", {"start": v(-451.86, -190.48) * mm, "end": v(-445.26, -201.91) * mm});
            skLineSegment(sketch, "E1249", {"start": v(-437.64, -196.83) * mm, "end": v(-444.24, -208.26) * mm});
            skLineSegment(sketch, "E1250", {"start": v(-444.24, -208.26) * mm, "end": v(-431.04, -208.26) * mm});
            skLineSegment(sketch, "E1251", {"start": v(-431.04, -208.26) * mm, "end": v(-437.64, -196.83) * mm});
            skLineSegment(sketch, "E1252", {"start": v(-452.88, -196.83) * mm, "end": v(-459.48, -208.26) * mm});
            skLineSegment(sketch, "E1253", {"start": v(-459.48, -208.26) * mm, "end": v(-446.28, -208.26) * mm});
            skLineSegment(sketch, "E1254", {"start": v(-446.28, -208.26) * mm, "end": v(-452.88, -196.83) * mm});
            skLineSegment(sketch, "E1255", {"start": v(-371.35, -176.51) * mm, "end": v(-377.95, -187.94) * mm});
            skLineSegment(sketch, "E1256", {"start": v(-377.95, -187.94) * mm, "end": v(-364.76, -187.94) * mm});
            skLineSegment(sketch, "E1257", {"start": v(-364.76, -187.94) * mm, "end": v(-371.35, -176.51) * mm});
            skLineSegment(sketch, "E1258", {"start": v(-378.97, -181.6) * mm, "end": v(-372.38, -170.16) * mm});
            skLineSegment(sketch, "E1259", {"start": v(-372.38, -170.16) * mm, "end": v(-385.57, -170.16) * mm});
            skLineSegment(sketch, "E1260", {"start": v(-385.57, -170.16) * mm, "end": v(-378.97, -181.6) * mm});
            skLineSegment(sketch, "E1261", {"start": v(-363.73, -181.6) * mm, "end": v(-357.14, -170.16) * mm});
            skLineSegment(sketch, "E1262", {"start": v(-357.14, -170.16) * mm, "end": v(-370.33, -170.16) * mm});
            skLineSegment(sketch, "E1263", {"start": v(-370.33, -170.16) * mm, "end": v(-363.73, -181.6) * mm});
            skLineSegment(sketch, "E1264", {"start": v(-396.75, -181.6) * mm, "end": v(-390.16, -170.16) * mm});
            skLineSegment(sketch, "E1265", {"start": v(-390.16, -170.16) * mm, "end": v(-403.35, -170.16) * mm});
            skLineSegment(sketch, "E1266", {"start": v(-403.35, -170.16) * mm, "end": v(-396.75, -181.6) * mm});
            skLineSegment(sketch, "E1267", {"start": v(-389.13, -176.51) * mm, "end": v(-395.73, -187.94) * mm});
            skLineSegment(sketch, "E1268", {"start": v(-395.73, -187.94) * mm, "end": v(-382.54, -187.94) * mm});
            skLineSegment(sketch, "E1269", {"start": v(-382.54, -187.94) * mm, "end": v(-389.13, -176.51) * mm});
            skLineSegment(sketch, "E1270", {"start": v(-404.37, -176.51) * mm, "end": v(-410.97, -187.94) * mm});
            skLineSegment(sketch, "E1271", {"start": v(-410.97, -187.94) * mm, "end": v(-397.78, -187.94) * mm});
            skLineSegment(sketch, "E1272", {"start": v(-397.78, -187.94) * mm, "end": v(-404.37, -176.51) * mm});
            skLineSegment(sketch, "E1273", {"start": v(-419.86, -176.51) * mm, "end": v(-426.46, -187.94) * mm});
            skLineSegment(sketch, "E1274", {"start": v(-426.46, -187.94) * mm, "end": v(-413.26, -187.94) * mm});
            skLineSegment(sketch, "E1275", {"start": v(-413.26, -187.94) * mm, "end": v(-419.86, -176.51) * mm});
            skLineSegment(sketch, "E1276", {"start": v(-427.48, -181.6) * mm, "end": v(-420.88, -170.16) * mm});
            skLineSegment(sketch, "E1277", {"start": v(-420.88, -170.16) * mm, "end": v(-434.08, -170.16) * mm});
            skLineSegment(sketch, "E1278", {"start": v(-434.08, -170.16) * mm, "end": v(-427.48, -181.6) * mm});
            skLineSegment(sketch, "E1279", {"start": v(-412.24, -181.6) * mm, "end": v(-405.64, -170.16) * mm});
            skLineSegment(sketch, "E1280", {"start": v(-405.64, -170.16) * mm, "end": v(-418.84, -170.16) * mm});
            skLineSegment(sketch, "E1281", {"start": v(-418.84, -170.16) * mm, "end": v(-412.24, -181.6) * mm});
            skLineSegment(sketch, "E1282", {"start": v(-445.26, -181.6) * mm, "end": v(-438.66, -170.16) * mm});
            skLineSegment(sketch, "E1283", {"start": v(-438.66, -170.16) * mm, "end": v(-451.86, -170.16) * mm});
            skLineSegment(sketch, "E1284", {"start": v(-451.86, -170.16) * mm, "end": v(-445.26, -181.6) * mm});
            skLineSegment(sketch, "E1285", {"start": v(-437.64, -176.51) * mm, "end": v(-444.24, -187.94) * mm});
            skLineSegment(sketch, "E1286", {"start": v(-444.24, -187.94) * mm, "end": v(-431.04, -187.94) * mm});
            skLineSegment(sketch, "E1287", {"start": v(-431.04, -187.94) * mm, "end": v(-437.64, -176.51) * mm});
            skLineSegment(sketch, "E1288", {"start": v(-452.88, -176.51) * mm, "end": v(-459.48, -187.94) * mm});
            skLineSegment(sketch, "E1289", {"start": v(-459.48, -187.94) * mm, "end": v(-446.28, -187.94) * mm});
            skLineSegment(sketch, "E1290", {"start": v(-446.28, -187.94) * mm, "end": v(-452.88, -176.51) * mm});
            skLineSegment(sketch, "E1291", {"start": v(-371.35, -217.15) * mm, "end": v(-377.95, -228.58) * mm});
            skLineSegment(sketch, "E1292", {"start": v(-377.95, -228.58) * mm, "end": v(-364.76, -228.58) * mm});
            skLineSegment(sketch, "E1293", {"start": v(-364.76, -228.58) * mm, "end": v(-371.35, -217.15) * mm});
            skLineSegment(sketch, "E1294", {"start": v(-378.97, -222.23) * mm, "end": v(-372.38, -210.8) * mm});
            skLineSegment(sketch, "E1295", {"start": v(-372.38, -210.8) * mm, "end": v(-385.57, -210.8) * mm});
            skLineSegment(sketch, "E1296", {"start": v(-385.57, -210.8) * mm, "end": v(-378.97, -222.23) * mm});
            skLineSegment(sketch, "E1297", {"start": v(-363.73, -222.23) * mm, "end": v(-357.14, -210.8) * mm});
            skLineSegment(sketch, "E1298", {"start": v(-357.14, -210.8) * mm, "end": v(-370.33, -210.8) * mm});
            skLineSegment(sketch, "E1299", {"start": v(-370.33, -210.8) * mm, "end": v(-363.73, -222.23) * mm});
            skLineSegment(sketch, "E1300", {"start": v(-396.75, -222.23) * mm, "end": v(-390.16, -210.8) * mm});
            skLineSegment(sketch, "E1301", {"start": v(-390.16, -210.8) * mm, "end": v(-403.35, -210.8) * mm});
            skLineSegment(sketch, "E1302", {"start": v(-403.35, -210.8) * mm, "end": v(-396.75, -222.23) * mm});
            skLineSegment(sketch, "E1303", {"start": v(-389.13, -217.15) * mm, "end": v(-395.73, -228.58) * mm});
            skLineSegment(sketch, "E1304", {"start": v(-395.73, -228.58) * mm, "end": v(-382.54, -228.58) * mm});
            skLineSegment(sketch, "E1305", {"start": v(-382.54, -228.58) * mm, "end": v(-389.13, -217.15) * mm});
            skLineSegment(sketch, "E1306", {"start": v(-404.37, -217.15) * mm, "end": v(-410.97, -228.58) * mm});
            skLineSegment(sketch, "E1307", {"start": v(-410.97, -228.58) * mm, "end": v(-397.78, -228.58) * mm});
            skLineSegment(sketch, "E1308", {"start": v(-397.78, -228.58) * mm, "end": v(-404.37, -217.15) * mm});
            skLineSegment(sketch, "E1309", {"start": v(-419.86, -217.15) * mm, "end": v(-426.46, -228.58) * mm});
            skLineSegment(sketch, "E1310", {"start": v(-426.46, -228.58) * mm, "end": v(-413.26, -228.58) * mm});
            skLineSegment(sketch, "E1311", {"start": v(-413.26, -228.58) * mm, "end": v(-419.86, -217.15) * mm});
            skLineSegment(sketch, "E1312", {"start": v(-427.48, -222.23) * mm, "end": v(-420.88, -210.8) * mm});
            skLineSegment(sketch, "E1313", {"start": v(-420.88, -210.8) * mm, "end": v(-434.08, -210.8) * mm});
            skLineSegment(sketch, "E1314", {"start": v(-434.08, -210.8) * mm, "end": v(-427.48, -222.23) * mm});
            skLineSegment(sketch, "E1315", {"start": v(-412.24, -222.23) * mm, "end": v(-405.64, -210.8) * mm});
            skLineSegment(sketch, "E1316", {"start": v(-405.64, -210.8) * mm, "end": v(-418.84, -210.8) * mm});
            skLineSegment(sketch, "E1317", {"start": v(-418.84, -210.8) * mm, "end": v(-412.24, -222.23) * mm});
            skLineSegment(sketch, "E1318", {"start": v(-445.26, -222.23) * mm, "end": v(-438.66, -210.8) * mm});
            skLineSegment(sketch, "E1319", {"start": v(-438.66, -210.8) * mm, "end": v(-451.86, -210.8) * mm});
            skLineSegment(sketch, "E1320", {"start": v(-451.86, -210.8) * mm, "end": v(-445.26, -222.23) * mm});
            skLineSegment(sketch, "E1321", {"start": v(-437.64, -217.15) * mm, "end": v(-444.24, -228.58) * mm});
            skLineSegment(sketch, "E1322", {"start": v(-444.24, -228.58) * mm, "end": v(-431.04, -228.58) * mm});
            skLineSegment(sketch, "E1323", {"start": v(-431.04, -228.58) * mm, "end": v(-437.64, -217.15) * mm});
            skLineSegment(sketch, "E1324", {"start": v(-446.28, -228.58) * mm, "end": v(-452.88, -217.15) * mm});
            skLineSegment(sketch, "E1325", {"start": v(-452.88, -217.15) * mm, "end": v(-459, -227.74) * mm});
            skLineSegment(sketch, "E1326", {"start": v(-457.63, -228.58) * mm, "end": v(-446.28, -228.58) * mm});
            skLineSegment(sketch, "E1327", {"start": v(-363.73, -140.95) * mm, "end": v(-357.96, -130.95) * mm});
            skCircle(sketch, "E1328", {"center": v(353.82, 431.82) * mm, "radius": 3.18 * mm});
            skLineSegment(sketch, "E1329", {"start": v(318.6, -9.8) * mm, "end": v(345.27, -9.8) * mm});
            skLineSegment(sketch, "E1330", {"start": v(345.27, -9.8) * mm, "end": v(345.27, 21.18) * mm});
            skLineSegment(sketch, "E1331", {"start": v(345.27, 21.18) * mm, "end": v(318.6, 21.18) * mm});
            skLineSegment(sketch, "E1332", {"start": v(318.6, 21.18) * mm, "end": v(318.6, -9.8) * mm});
            skCircle(sketch, "E1333", {"center": v(291.14, 0.86) * mm, "radius": 1.59 * mm});
            skCircle(sketch, "E1334", {"center": v(262.57, 0.86) * mm, "radius": 1.59 * mm});
            skLineSegment(sketch, "E1335", {"start": v(268.85, 7.51) * mm, "end": v(268.85, -5.8) * mm});
            skLineSegment(sketch, "E1336", {"start": v(268.85, -5.8) * mm, "end": v(284.85, -5.8) * mm});
            skLineSegment(sketch, "E1337", {"start": v(284.85, -5.8) * mm, "end": v(284.85, 7.51) * mm});
            skLineSegment(sketch, "E1338", {"start": v(284.85, 7.51) * mm, "end": v(268.85, 7.51) * mm});
            skCircle(sketch, "E1339", {"center": v(291.14, 16.1) * mm, "radius": 1.42 * mm});
            skCircle(sketch, "E1340", {"center": v(262.57, 16.1) * mm, "radius": 1.42 * mm});
            skLineSegment(sketch, "E1341", {"start": v(270.35, 13.75) * mm, "end": v(283.36, 13.75) * mm});
            skLineSegment(sketch, "E1342", {"start": v(283.36, 13.75) * mm, "end": v(283.36, 18.45) * mm});
            skLineSegment(sketch, "E1343", {"start": v(283.36, 18.45) * mm, "end": v(270.35, 18.45) * mm});
            skLineSegment(sketch, "E1344", {"start": v(270.35, 18.45) * mm, "end": v(270.35, 13.75) * mm});
            skLineSegment(sketch, "E1345", {"start": v(377.9, -411.06) * mm, "end": v(367.14, -411.06) * mm});
            skLineSegment(sketch, "E1346", {"start": v(377.9, -411.06) * mm, "end": v(377.9, -401.36) * mm});
            skLineSegment(sketch, "E1347", {"start": v(377.9, -401.36) * mm, "end": v(-511.1, -401.36) * mm});
            skLineSegment(sketch, "E1348", {"start": v(-500.36, -411.06) * mm, "end": v(-511.1, -411.06) * mm});
            skLineSegment(sketch, "E1349", {"start": v(-511.1, -411.06) * mm, "end": v(-511.1, -401.36) * mm});
            skLineSegment(sketch, "E1350", {"start": v(-522.48, -16.04) * mm, "end": v(-511.73, -16.04) * mm});
            skLineSegment(sketch, "E1351", {"start": v(-522.48, -16.04) * mm, "end": v(-522.48, -25.74) * mm});
            skLineSegment(sketch, "E1352", {"start": v(355.76, -16.04) * mm, "end": v(366.52, -16.04) * mm});
            skLineSegment(sketch, "E1353", {"start": v(366.52, -16.04) * mm, "end": v(366.52, -25.74) * mm});
            skLineSegment(sketch, "E1354", {"start": v(-522.48, -25.74) * mm, "end": v(366.52, -25.74) * mm});
            skCircle(sketch, "E1355", {"center": v(-52.58, 5.1) * mm, "radius": 1.59 * mm});
            skCircle(sketch, "E1356", {"center": v(-52.58, -5.06) * mm, "radius": 1.59 * mm});
            skCircle(sketch, "E1357", {"center": v(-52.58, 17.8) * mm, "radius": 1.59 * mm});
            skArc(sketch, "E1358", {"start": v(-0.51, 455.51) * mm, "mid": v(10.92, 444.08) * mm, "end": v(22.35, 455.51) * mm});
            skLineSegment(sketch, "E1359", {"start": v(-358.57, 455.51) * mm, "end": v(-0.51, 455.51) * mm});
            skLineSegment(sketch, "E1360", {"start": v(22.35, 455.51) * mm, "end": v(380.4, 455.51) * mm});
            skCircle(sketch, "E1361", {"center": v(28.7, 449.6) * mm, "radius": 2.18 * mm});
            skCircle(sketch, "E1362", {"center": v(-6.86, 449.6) * mm, "radius": 2.18 * mm});
            skCircle(sketch, "E1363", {"center": v(-34.8, 17.8) * mm, "radius": 2.18 * mm});
            skCircle(sketch, "E1364", {"center": v(-70.36, 17.8) * mm, "radius": 2.18 * mm});
            skCircle(sketch, "E1365", {"center": v(-394.85, 365.97) * mm, "radius": 2.04 * mm});
            skCircle(sketch, "E1366", {"center": v(-394.85, 240.25) * mm, "radius": 2.04 * mm});
            skCircle(sketch, "E1367", {"center": v(-269.12, 240.25) * mm, "radius": 2.04 * mm});
            skCircle(sketch, "E1368", {"center": v(-269.12, 365.97) * mm, "radius": 2.04 * mm});
            skCircle(sketch, "E1369", {"center": v(290.95, 365.97) * mm, "radius": 2.04 * mm});
            skCircle(sketch, "E1370", {"center": v(290.95, 240.25) * mm, "radius": 2.04 * mm});
            skCircle(sketch, "E1371", {"center": v(416.68, 240.25) * mm, "radius": 2.04 * mm});
            skCircle(sketch, "E1372", {"center": v(416.68, 365.97) * mm, "radius": 2.04 * mm});
            skCircle(sketch, "E1373", {"center": v(-166.25, 365.97) * mm, "radius": 2.04 * mm});
            skCircle(sketch, "E1374", {"center": v(-166.25, 240.25) * mm, "radius": 2.04 * mm});
            skCircle(sketch, "E1375", {"center": v(-40.52, 240.25) * mm, "radius": 2.04 * mm});
            skCircle(sketch, "E1376", {"center": v(-40.52, 365.97) * mm, "radius": 2.04 * mm});
            skArc(sketch, "E1377", {"start": v(-334.14, 310.42) * mm, "mid": v(-331.98, 295.5) * mm, "end": v(-329.83, 310.42) * mm});
            skArc(sketch, "E1378", {"start": v(-329.83, 360.7) * mm, "mid": v(-331.98, 361.53) * mm, "end": v(-334.14, 360.7) * mm});
            skLineSegment(sketch, "E1379", {"start": v(-334.14, 360.7) * mm, "end": v(-334.14, 310.42) * mm});
            skLineSegment(sketch, "E1380", {"start": v(-329.83, 310.42) * mm, "end": v(-329.83, 360.7) * mm});
            skArc(sketch, "E1381", {"start": v(-105.54, 310.42) * mm, "mid": v(-103.38, 295.5) * mm, "end": v(-101.23, 310.42) * mm});
            skArc(sketch, "E1382", {"start": v(-101.23, 360.7) * mm, "mid": v(-103.38, 361.53) * mm, "end": v(-105.54, 360.7) * mm});
            skLineSegment(sketch, "E1383", {"start": v(-105.54, 360.7) * mm, "end": v(-105.54, 310.42) * mm});
            skLineSegment(sketch, "E1384", {"start": v(-101.23, 310.42) * mm, "end": v(-101.23, 360.7) * mm});
            skArc(sketch, "E1385", {"start": v(351.66, 310.42) * mm, "mid": v(353.82, 295.5) * mm, "end": v(355.97, 310.42) * mm});
            skArc(sketch, "E1386", {"start": v(355.97, 360.7) * mm, "mid": v(353.82, 361.53) * mm, "end": v(351.66, 360.7) * mm});
            skLineSegment(sketch, "E1387", {"start": v(351.66, 360.7) * mm, "end": v(351.66, 310.42) * mm});
            skLineSegment(sketch, "E1388", {"start": v(355.97, 310.42) * mm, "end": v(355.97, 360.7) * mm});
            skArc(sketch, "E1389", {"start": v(123.06, 314.86) * mm, "mid": v(125.22, 299.93) * mm, "end": v(127.37, 314.86) * mm});
            skArc(sketch, "E1390", {"start": v(127.37, 365.14) * mm, "mid": v(125.22, 365.97) * mm, "end": v(123.06, 365.14) * mm});
            skLineSegment(sketch, "E1391", {"start": v(123.06, 365.14) * mm, "end": v(123.06, 314.86) * mm});
            skLineSegment(sketch, "E1392", {"start": v(127.37, 314.86) * mm, "end": v(127.37, 365.14) * mm});
            skSolve(sketch);
        }
        {
            var Q0;
            Q0 = qSketchRegion(id + "F0", true);
            extrude(context, id + "F1", {"entities" : qUnion([Q0]), "depth" : 1 / 203.2 * mm});
        }
    });
